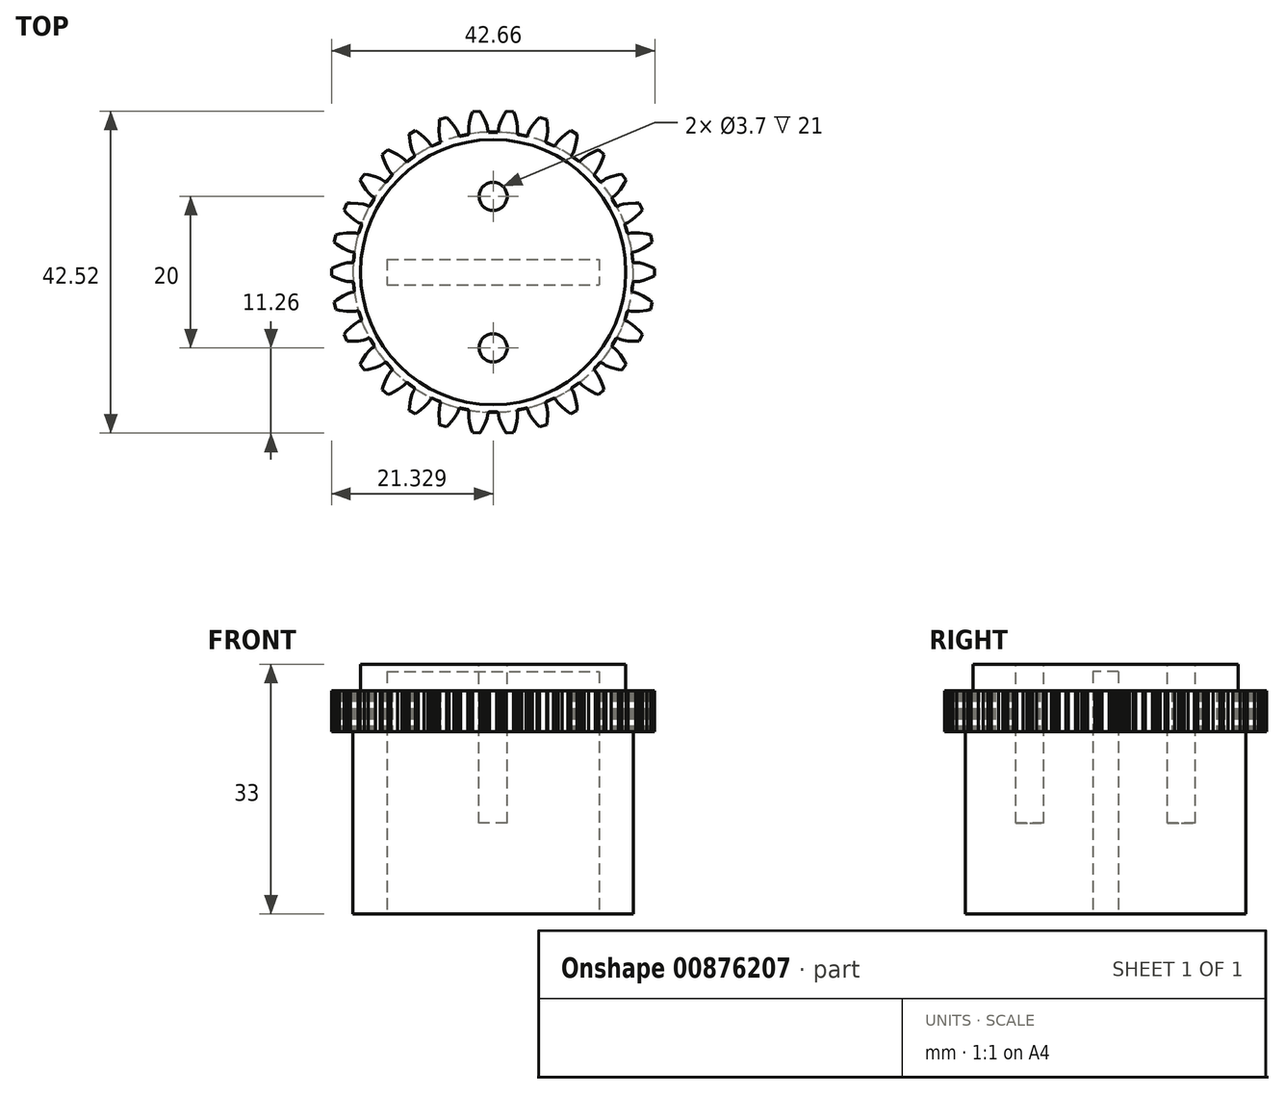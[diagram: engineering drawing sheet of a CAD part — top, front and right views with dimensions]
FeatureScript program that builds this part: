
annotation { "Feature Type Name" : "Feature", "Feature Type Description" : "" }
export const myFeature = defineFeature(function(context is Context, id is Id, definition is map)
    precondition{}
    {
        {
            var Q0;
            Q0=qCreatedBy(makeId("Top.planeOp"),FACE);
            var sketch = newSketch(context, id + "F0", { "sketchPlane" : qUnion([Q0])});
            skLineSegment(sketch, "E0", {"start": v(5.95, 16.64) * mm, "end": v(6.04, 16.7) * mm});
            skLineSegment(sketch, "E1", {"start": v(6.04, 16.7) * mm, "end": v(6.12, 16.74) * mm});
            skLineSegment(sketch, "E2", {"start": v(21.02, -17.09) * mm, "end": v(21.05, -17.07) * mm});
            skLineSegment(sketch, "E3", {"start": v(32.31, -2.53) * mm, "end": v(32.33, -2.41) * mm});
            skLineSegment(sketch, "E4", {"start": v(32.33, -2.41) * mm, "end": v(32.35, -2.32) * mm});
            skLineSegment(sketch, "E5", {"start": v(6.12, 16.74) * mm, "end": v(6.43, 16.86) * mm});
            skLineSegment(sketch, "E6", {"start": v(6.43, 16.86) * mm, "end": v(6.95, 17.06) * mm});
            skLineSegment(sketch, "E7", {"start": v(6.13, -16.74) * mm, "end": v(6.43, -16.86) * mm});
            skLineSegment(sketch, "E8", {"start": v(6.43, -16.86) * mm, "end": v(6.95, -17.06) * mm});
            skLineSegment(sketch, "E9", {"start": v(17.47, -18.17) * mm, "end": v(17.79, -18.09) * mm});
            skLineSegment(sketch, "E10", {"start": v(17.79, -18.09) * mm, "end": v(18.32, -17.95) * mm});
            skLineSegment(sketch, "E11", {"start": v(21.86, -16.75) * mm, "end": v(21.96, -16.7) * mm});
            skLineSegment(sketch, "E12", {"start": v(21.96, -16.7) * mm, "end": v(22.05, -16.64) * mm});
            skLineSegment(sketch, "E13", {"start": v(10.18, 18.1) * mm, "end": v(10.52, 18.17) * mm});
            skLineSegment(sketch, "E14", {"start": v(-4.35, 2.32) * mm, "end": v(-4.34, 2.41) * mm});
            skLineSegment(sketch, "E15", {"start": v(-4.34, 2.41) * mm, "end": v(-4.31, 2.53) * mm});
            skLineSegment(sketch, "E16", {"start": v(10.53, -18.17) * mm, "end": v(10.63, -18.18) * mm});
            skLineSegment(sketch, "E17", {"start": v(10.63, -18.18) * mm, "end": v(10.73, -18.2) * mm});
            skLineSegment(sketch, "E18", {"start": v(32.37, 1.98) * mm, "end": v(32.35, 2.27) * mm});
            skLineSegment(sketch, "E19", {"start": v(10.18, -18.1) * mm, "end": v(10.53, -18.17) * mm});
            skLineSegment(sketch, "E20", {"start": v(27.49, -12.66) * mm, "end": v(27.7, -12.4) * mm});
            skLineSegment(sketch, "E21", {"start": v(27.7, -12.4) * mm, "end": v(28.05, -11.98) * mm});
            skLineSegment(sketch, "E22", {"start": v(21.02, 17.09) * mm, "end": v(21.05, 17.07) * mm});
            skLineSegment(sketch, "E23", {"start": v(32.35, -2.27) * mm, "end": v(32.37, -1.98) * mm});
            skLineSegment(sketch, "E24", {"start": v(32.33, 2.41) * mm, "end": v(32.31, 2.52) * mm});
            skLineSegment(sketch, "E25", {"start": v(17.26, 18.2) * mm, "end": v(17.37, 18.18) * mm});
            skLineSegment(sketch, "E26", {"start": v(17.47, 18.17) * mm, "end": v(17.79, 18.09) * mm});
            skLineSegment(sketch, "E27", {"start": v(17.79, 18.09) * mm, "end": v(18.32, 17.95) * mm});
            skLineSegment(sketch, "E28", {"start": v(19.8, -20.1) * mm, "end": v(20.12, -20.44) * mm});
            skLineSegment(sketch, "E29", {"start": v(22.35, -17) * mm, "end": v(22.6, -17.33) * mm});
            skLineSegment(sketch, "E30", {"start": v(28.5, -15.07) * mm, "end": v(28.64, -15.52) * mm});
            skLineSegment(sketch, "E31", {"start": v(5.65, -17) * mm, "end": v(5.77, -16.76) * mm});
            skLineSegment(sketch, "E32", {"start": v(27.4, -13) * mm, "end": v(27.58, -13.2) * mm});
            skLineSegment(sketch, "E33", {"start": v(17.23, 18.66) * mm, "end": v(17.22, 19.08) * mm});
            skLineSegment(sketch, "E34", {"start": v(28.64, -15.52) * mm, "end": v(27.9, -16.18) * mm});
            skLineSegment(sketch, "E35", {"start": v(27.34, -12.9) * mm, "end": v(27.4, -13) * mm});
            skLineSegment(sketch, "E36", {"start": v(27.47, -16) * mm, "end": v(26.6, -15.55) * mm});
            skLineSegment(sketch, "E37", {"start": v(26.02, -15.16) * mm, "end": v(25.7, -14.88) * mm});
            skLineSegment(sketch, "E38", {"start": v(10.8, -18.28) * mm, "end": v(10.8, -18.4) * mm});
            skLineSegment(sketch, "E39", {"start": v(27.9, -16.18) * mm, "end": v(27.47, -16) * mm});
            skLineSegment(sketch, "E40", {"start": v(26.6, -15.55) * mm, "end": v(26.02, -15.16) * mm});
            skLineSegment(sketch, "E41", {"start": v(10.73, -18.2) * mm, "end": v(10.8, -18.28) * mm});
            skLineSegment(sketch, "E42", {"start": v(10.73, -18.2) * mm, "end": v(10.63, -18.15) * mm});
            skLineSegment(sketch, "E43", {"start": v(13.41, -18.48) * mm, "end": v(13.33, -18.55) * mm});
            skLineSegment(sketch, "E44", {"start": v(30.5, -8.72) * mm, "end": v(30.4, -8.7) * mm});
            skLineSegment(sketch, "E45", {"start": v(18.56, -18.1) * mm, "end": v(18.64, -18.36) * mm});
            skLineSegment(sketch, "E46", {"start": v(24.7, -16.12) * mm, "end": v(24.9, -16.8) * mm});
            skLineSegment(sketch, "E47", {"start": v(-5.77, -3.14) * mm, "end": v(-5.14, -2.83) * mm});
            skLineSegment(sketch, "E48", {"start": v(34.3, -5.02) * mm, "end": v(33.33, -5.17) * mm});
            skLineSegment(sketch, "E49", {"start": v(12.95, 19.99) * mm, "end": v(13.18, 19.33) * mm});
            skLineSegment(sketch, "E50", {"start": v(12.26, 21.26) * mm, "end": v(12.5, 20.86) * mm});
            skLineSegment(sketch, "E51", {"start": v(12.5, 20.86) * mm, "end": v(12.95, 19.99) * mm});
            skLineSegment(sketch, "E52", {"start": v(33.33, -5.17) * mm, "end": v(32.63, -5.2) * mm});
            skLineSegment(sketch, "E53", {"start": v(32.63, -5.2) * mm, "end": v(32.22, -5.16) * mm});
            skLineSegment(sketch, "E54", {"start": v(28.9, -12.33) * mm, "end": v(28.54, -12.12) * mm});
            skLineSegment(sketch, "E55", {"start": v(13.28, 18.92) * mm, "end": v(13.18, 19.33) * mm});
            skLineSegment(sketch, "E56", {"start": v(0.6, -12.7) * mm, "end": v(0.66, -12.8) * mm});
            skLineSegment(sketch, "E57", {"start": v(15.5, -20.86) * mm, "end": v(15.74, -21.26) * mm});
            skLineSegment(sketch, "E58", {"start": v(16.72, -21.16) * mm, "end": v(15.74, -21.26) * mm});
            skLineSegment(sketch, "E59", {"start": v(15.05, -19.99) * mm, "end": v(15.5, -20.86) * mm});
            skLineSegment(sketch, "E60", {"start": v(28.33, -11.96) * mm, "end": v(28.23, -11.92) * mm});
            skLineSegment(sketch, "E61", {"start": v(27.82, 13.54) * mm, "end": v(27.58, 13.2) * mm});
            skLineSegment(sketch, "E62", {"start": v(28.54, -12.12) * mm, "end": v(28.33, -11.96) * mm});
            skLineSegment(sketch, "E63", {"start": v(9.44, 18.1) * mm, "end": v(9.36, 18.36) * mm});
            skLineSegment(sketch, "E64", {"start": v(10.78, 19.08) * mm, "end": v(10.77, 18.66) * mm});
            skLineSegment(sketch, "E65", {"start": v(10.8, -18.4) * mm, "end": v(10.77, -18.66) * mm});
            skLineSegment(sketch, "E66", {"start": v(-4.3, -2.4) * mm, "end": v(-4.31, -2.52) * mm});
            skLineSegment(sketch, "E67", {"start": v(17.47, -18.17) * mm, "end": v(17.26, -18.2) * mm});
            skLineSegment(sketch, "E68", {"start": v(-4.36, -2.32) * mm, "end": v(-4.31, -2.52) * mm});
            skLineSegment(sketch, "E69", {"start": v(21.86, 16.75) * mm, "end": v(22.05, 16.64) * mm});
            skLineSegment(sketch, "E70", {"start": v(-4.36, -2.32) * mm, "end": v(-4.44, -1.35) * mm});
            skLineSegment(sketch, "E71", {"start": v(0.51, -12.66) * mm, "end": v(-0.12, -11.93) * mm});
            skLineSegment(sketch, "E72", {"start": v(30.21, -8.91) * mm, "end": v(29.7, -9.75) * mm});
            skLineSegment(sketch, "E73", {"start": v(30.5, 1.75) * mm, "end": v(30.5, -1.75) * mm, "construction": true});
            skLineSegment(sketch, "E74", {"start": v(27.48, 12.66) * mm, "end": v(27.34, 12.8) * mm});
            skLineSegment(sketch, "E75", {"start": v(0.51, 12.66) * mm, "end": v(0.66, 12.8) * mm});
            skLineSegment(sketch, "E76", {"start": v(27.49, -12.66) * mm, "end": v(27.34, -12.8) * mm});
            skLineSegment(sketch, "E77", {"start": v(-2.5, -1.75) * mm, "end": v(-2.5, 1.75) * mm, "construction": true});
            skLineSegment(sketch, "E78", {"start": v(-2.21, 8.9) * mm, "end": v(-1.7, 9.75) * mm});
            skLineSegment(sketch, "E79", {"start": v(0.51, -12.66) * mm, "end": v(0.66, -12.8) * mm});
            skLineSegment(sketch, "E80", {"start": v(30.21, 8.9) * mm, "end": v(29.74, 9.64) * mm});
            skLineSegment(sketch, "E81", {"start": v(30.21, -8.91) * mm, "end": v(30.3, -8.73) * mm});
            skLineSegment(sketch, "E82", {"start": v(10.52, 18.17) * mm, "end": v(10.73, 18.2) * mm});
            skLineSegment(sketch, "E83", {"start": v(17.23, -18.66) * mm, "end": v(17.2, -18.4) * mm});
            skLineSegment(sketch, "E84", {"start": v(-3.54, -12.14) * mm, "end": v(-3.32, -11.73) * mm});
            skLineSegment(sketch, "E85", {"start": v(30.4, 8.7) * mm, "end": v(30.5, 8.72) * mm});
            skLineSegment(sketch, "E86", {"start": v(-2.97, -12.93) * mm, "end": v(-3.54, -12.14) * mm});
            skLineSegment(sketch, "E87", {"start": v(-5.68, 8.23) * mm, "end": v(-5.38, 7.87) * mm});
            skLineSegment(sketch, "E88", {"start": v(21.12, 19.67) * mm, "end": v(21.17, 18.69) * mm});
            skLineSegment(sketch, "E89", {"start": v(9.36, 18.36) * mm, "end": v(9.18, 18.74) * mm});
            skLineSegment(sketch, "E90", {"start": v(-4.69, 7.18) * mm, "end": v(-5.38, 7.87) * mm});
            skLineSegment(sketch, "E91", {"start": v(31.85, 5.1) * mm, "end": v(31.96, 5.1) * mm});
            skLineSegment(sketch, "E92", {"start": v(-2.97, 12.93) * mm, "end": v(-2.5, 12.85) * mm});
            skLineSegment(sketch, "E93", {"start": v(28.23, -11.92) * mm, "end": v(28.12, -11.93) * mm});
            skLineSegment(sketch, "E94", {"start": v(34.6, 3.67) * mm, "end": v(33.77, 3.14) * mm});
            skLineSegment(sketch, "E95", {"start": v(31.39, -6.27) * mm, "end": v(31.43, -6.37) * mm});
            skLineSegment(sketch, "E96", {"start": v(12.95, -19.99) * mm, "end": v(12.5, -20.86) * mm});
            skLineSegment(sketch, "E97", {"start": v(10.63, 18.15) * mm, "end": v(10.73, 18.2) * mm});
            skLineSegment(sketch, "E98", {"start": v(3.3, 16.12) * mm, "end": v(3.46, 15.73) * mm});
            skLineSegment(sketch, "E99", {"start": v(21.12, 18) * mm, "end": v(21.04, 17.58) * mm});
            skLineSegment(sketch, "E100", {"start": v(34.96, 3.95) * mm, "end": v(34.6, 3.67) * mm});
            skLineSegment(sketch, "E101", {"start": v(-4.31, 2.53) * mm, "end": v(-4.3, 2.4) * mm});
            skLineSegment(sketch, "E102", {"start": v(20.95, -17.33) * mm, "end": v(20.93, -17.22) * mm});
            skLineSegment(sketch, "E103", {"start": v(24.4, -15.5) * mm, "end": v(24.36, -15.4) * mm});
            skLineSegment(sketch, "E104", {"start": v(9.36, -18.36) * mm, "end": v(9.44, -18.1) * mm});
            skLineSegment(sketch, "E105", {"start": v(13.28, -18.92) * mm, "end": v(13.3, -18.65) * mm});
            skLineSegment(sketch, "E106", {"start": v(17.2, -18.4) * mm, "end": v(17.2, -18.28) * mm});
            skLineSegment(sketch, "E107", {"start": v(27.39, 12.7) * mm, "end": v(27.34, 12.8) * mm});
            skLineSegment(sketch, "E108", {"start": v(5.65, 17) * mm, "end": v(5.4, 17.33) * mm});
            skLineSegment(sketch, "E109", {"start": v(17.2, 18.28) * mm, "end": v(17.2, 18.4) * mm});
            skLineSegment(sketch, "E110", {"start": v(10.7, 17.33) * mm, "end": v(8.55, 16.78) * mm});
            skLineSegment(sketch, "E111", {"start": v(17.3, 17.33) * mm, "end": v(15.1, 17.6) * mm});
            skLineSegment(sketch, "E112", {"start": v(8.55, 16.78) * mm, "end": v(6.49, 15.96) * mm});
            skLineSegment(sketch, "E113", {"start": v(15.1, 17.6) * mm, "end": v(12.9, 17.6) * mm});
            skLineSegment(sketch, "E114", {"start": v(19.45, 16.78) * mm, "end": v(17.3, 17.33) * mm});
            skLineSegment(sketch, "E115", {"start": v(12.9, 17.6) * mm, "end": v(10.7, 17.33) * mm});
            skLineSegment(sketch, "E116", {"start": v(23.1, 17.83) * mm, "end": v(22.6, 17.33) * mm});
            skLineSegment(sketch, "E117", {"start": v(20.93, 17.22) * mm, "end": v(20.95, 17.33) * mm});
            skLineSegment(sketch, "E118", {"start": v(30.5, 1.75) * mm, "end": v(-2.5, 1.75) * mm, "construction": true});
            skLineSegment(sketch, "E119", {"start": v(22.05, 16.64) * mm, "end": v(21.94, 16.66) * mm});
            skLineSegment(sketch, "E120", {"start": v(22.6, 17.33) * mm, "end": v(22.35, 17) * mm});
            skLineSegment(sketch, "E121", {"start": v(-2.5, -1.75) * mm, "end": v(30.5, -1.75) * mm, "construction": true});
            skLineSegment(sketch, "E122", {"start": v(21.94, 16.66) * mm, "end": v(21.05, 17.07) * mm});
            skLineSegment(sketch, "E123", {"start": v(22.15, 16.67) * mm, "end": v(22.05, 16.64) * mm});
            skLineSegment(sketch, "E124", {"start": v(22.22, 16.76) * mm, "end": v(22.15, 16.67) * mm});
            skLineSegment(sketch, "E125", {"start": v(22.35, 17) * mm, "end": v(22.22, 16.76) * mm});
            skLineSegment(sketch, "E126", {"start": v(20.98, 17.12) * mm, "end": v(20.93, 17.22) * mm});
            skLineSegment(sketch, "E127", {"start": v(23.85, 18.45) * mm, "end": v(23.1, 17.83) * mm});
            skLineSegment(sketch, "E128", {"start": v(24.24, 18.72) * mm, "end": v(23.85, 18.45) * mm});
            skLineSegment(sketch, "E129", {"start": v(26.02, 15.16) * mm, "end": v(25.7, 14.88) * mm});
            skLineSegment(sketch, "E130", {"start": v(26.6, 15.55) * mm, "end": v(26.02, 15.16) * mm});
            skLineSegment(sketch, "E131", {"start": v(24.38, 15.3) * mm, "end": v(24.36, 15.4) * mm});
            skLineSegment(sketch, "E132", {"start": v(25.05, 17.76) * mm, "end": v(25.09, 18.22) * mm});
            skLineSegment(sketch, "E133", {"start": v(24.54, 15.73) * mm, "end": v(24.7, 16.12) * mm});
            skLineSegment(sketch, "E134", {"start": v(24.36, 15.4) * mm, "end": v(24.4, 15.5) * mm});
            skLineSegment(sketch, "E135", {"start": v(24.4, 15.5) * mm, "end": v(24.54, 15.73) * mm});
            skLineSegment(sketch, "E136", {"start": v(24.9, 16.8) * mm, "end": v(25.05, 17.76) * mm});
            skLineSegment(sketch, "E137", {"start": v(25.23, 14.64) * mm, "end": v(24.46, 15.21) * mm});
            skLineSegment(sketch, "E138", {"start": v(25.09, 18.22) * mm, "end": v(24.24, 18.72) * mm});
            skLineSegment(sketch, "E139", {"start": v(24.7, 16.12) * mm, "end": v(24.9, 16.8) * mm});
            skLineSegment(sketch, "E140", {"start": v(25.44, 14.62) * mm, "end": v(25.33, 14.6) * mm});
            skLineSegment(sketch, "E141", {"start": v(25.53, 14.68) * mm, "end": v(25.44, 14.62) * mm});
            skLineSegment(sketch, "E142", {"start": v(25.7, 14.88) * mm, "end": v(25.53, 14.68) * mm});
            skLineSegment(sketch, "E143", {"start": v(-2.33, -10.37) * mm, "end": v(-2.78, -10.9) * mm});
            skLineSegment(sketch, "E144", {"start": v(21.12, 19.67) * mm, "end": v(21.06, 20.13) * mm});
            skLineSegment(sketch, "E145", {"start": v(-2.03, -10.08) * mm, "end": v(-2.33, -10.37) * mm});
            skLineSegment(sketch, "E146", {"start": v(20.95, 17.33) * mm, "end": v(21.04, 17.58) * mm});
            skLineSegment(sketch, "E147", {"start": v(3.64, -15.4) * mm, "end": v(3.6, -15.5) * mm});
            skLineSegment(sketch, "E148", {"start": v(13.18, -19.33) * mm, "end": v(13.28, -18.92) * mm});
            skLineSegment(sketch, "E149", {"start": v(27.47, 16) * mm, "end": v(26.6, 15.55) * mm});
            skLineSegment(sketch, "E150", {"start": v(6.95, -17.06) * mm, "end": v(7.02, -17.12) * mm});
            skLineSegment(sketch, "E151", {"start": v(32.68, -7.18) * mm, "end": v(32.13, -6.75) * mm});
            skLineSegment(sketch, "E152", {"start": v(19.8, 20.1) * mm, "end": v(19.19, 19.33) * mm});
            skLineSegment(sketch, "E153", {"start": v(20.12, 20.44) * mm, "end": v(19.8, 20.1) * mm});
            skLineSegment(sketch, "E154", {"start": v(32.13, -6.75) * mm, "end": v(31.77, -6.53) * mm});
            skLineSegment(sketch, "E155", {"start": v(21.06, 20.13) * mm, "end": v(20.12, 20.44) * mm});
            skLineSegment(sketch, "E156", {"start": v(21.12, 18) * mm, "end": v(21.17, 18.69) * mm});
            skLineSegment(sketch, "E157", {"start": v(13.3, -18.65) * mm, "end": v(13.33, -18.55) * mm});
            skLineSegment(sketch, "E158", {"start": v(21.94, -16.66) * mm, "end": v(22.05, -16.64) * mm});
            skLineSegment(sketch, "E159", {"start": v(-1.8, -9.93) * mm, "end": v(-2.03, -10.08) * mm});
            skLineSegment(sketch, "E160", {"start": v(18.64, 18.36) * mm, "end": v(18.56, 18.1) * mm});
            skLineSegment(sketch, "E161", {"start": v(22.05, -16.64) * mm, "end": v(22.15, -16.67) * mm});
            skLineSegment(sketch, "E162", {"start": v(18.82, 18.74) * mm, "end": v(18.64, 18.36) * mm});
            skLineSegment(sketch, "E163", {"start": v(7.02, -17.12) * mm, "end": v(7.06, -17.22) * mm});
            skLineSegment(sketch, "E164", {"start": v(17.36, 18.15) * mm, "end": v(17.26, 18.2) * mm});
            skLineSegment(sketch, "E165", {"start": v(17.2, -18.28) * mm, "end": v(17.26, -18.2) * mm});
            skLineSegment(sketch, "E166", {"start": v(19.19, 19.33) * mm, "end": v(18.82, 18.74) * mm});
            skLineSegment(sketch, "E167", {"start": v(18.42, 17.95) * mm, "end": v(18.32, 17.95) * mm});
            skLineSegment(sketch, "E168", {"start": v(18.5, 18) * mm, "end": v(18.42, 17.95) * mm});
            skLineSegment(sketch, "E169", {"start": v(18.56, 18.1) * mm, "end": v(18.5, 18) * mm});
            skLineSegment(sketch, "E170", {"start": v(22.15, -16.67) * mm, "end": v(22.22, -16.76) * mm});
            skLineSegment(sketch, "E171", {"start": v(33.38, -7.87) * mm, "end": v(32.68, -7.18) * mm});
            skLineSegment(sketch, "E172", {"start": v(17.26, 18.2) * mm, "end": v(17.2, 18.28) * mm});
            skLineSegment(sketch, "E173", {"start": v(21.05, -17.07) * mm, "end": v(21.94, -16.66) * mm});
            skLineSegment(sketch, "E174", {"start": v(21.04, -17.58) * mm, "end": v(20.95, -17.33) * mm});
            skLineSegment(sketch, "E175", {"start": v(21.17, -18.69) * mm, "end": v(21.12, -18) * mm});
            skLineSegment(sketch, "E176", {"start": v(17.2, 18.4) * mm, "end": v(17.23, 18.66) * mm});
            skLineSegment(sketch, "E177", {"start": v(20.93, -17.22) * mm, "end": v(20.98, -17.12) * mm});
            skLineSegment(sketch, "E178", {"start": v(14.48, 18.45) * mm, "end": v(13.52, 18.45) * mm});
            skLineSegment(sketch, "E179", {"start": v(14.7, 18.65) * mm, "end": v(14.67, 18.55) * mm});
            skLineSegment(sketch, "E180", {"start": v(14.72, 18.92) * mm, "end": v(14.7, 18.65) * mm});
            skLineSegment(sketch, "E181", {"start": v(14.81, 19.33) * mm, "end": v(14.72, 18.92) * mm});
            skLineSegment(sketch, "E182", {"start": v(15.05, 19.99) * mm, "end": v(14.81, 19.33) * mm});
            skLineSegment(sketch, "E183", {"start": v(21.12, -18) * mm, "end": v(21.04, -17.58) * mm});
            skLineSegment(sketch, "E184", {"start": v(14.67, 18.55) * mm, "end": v(14.59, 18.48) * mm});
            skLineSegment(sketch, "E185", {"start": v(25.09, -18.22) * mm, "end": v(25.05, -17.76) * mm});
            skLineSegment(sketch, "E186", {"start": v(16.87, 20.72) * mm, "end": v(16.72, 21.16) * mm});
            skLineSegment(sketch, "E187", {"start": v(13.3, 18.65) * mm, "end": v(13.28, 18.92) * mm});
            skLineSegment(sketch, "E188", {"start": v(31.75, -5.15) * mm, "end": v(31.85, -5.1) * mm});
            skLineSegment(sketch, "E189", {"start": v(11.12, 20.72) * mm, "end": v(10.87, 19.77) * mm});
            skLineSegment(sketch, "E190", {"start": v(12.26, 21.26) * mm, "end": v(11.28, 21.16) * mm});
            skLineSegment(sketch, "E191", {"start": v(10.87, 19.77) * mm, "end": v(10.78, 19.08) * mm});
            skLineSegment(sketch, "E192", {"start": v(33.68, -8.23) * mm, "end": v(33.38, -7.87) * mm});
            skLineSegment(sketch, "E193", {"start": v(15.74, 21.26) * mm, "end": v(15.5, 20.86) * mm});
            skLineSegment(sketch, "E194", {"start": v(17.12, 19.77) * mm, "end": v(16.87, 20.72) * mm});
            skLineSegment(sketch, "E195", {"start": v(11.28, 21.16) * mm, "end": v(11.12, 20.72) * mm});
            skLineSegment(sketch, "E196", {"start": v(15.5, 20.86) * mm, "end": v(15.05, 19.99) * mm});
            skLineSegment(sketch, "E197", {"start": v(13.33, 18.55) * mm, "end": v(13.3, 18.65) * mm});
            skLineSegment(sketch, "E198", {"start": v(16.72, 21.16) * mm, "end": v(15.74, 21.26) * mm});
            skLineSegment(sketch, "E199", {"start": v(11.28, -21.16) * mm, "end": v(12.26, -21.26) * mm});
            skLineSegment(sketch, "E200", {"start": v(27.34, -12.8) * mm, "end": v(27.39, -12.7) * mm});
            skLineSegment(sketch, "E201", {"start": v(10.8, 18.28) * mm, "end": v(10.73, 18.2) * mm});
            skLineSegment(sketch, "E202", {"start": v(10.8, 18.4) * mm, "end": v(10.8, 18.28) * mm});
            skLineSegment(sketch, "E203", {"start": v(11.12, -20.72) * mm, "end": v(11.28, -21.16) * mm});
            skLineSegment(sketch, "E204", {"start": v(10.77, 18.66) * mm, "end": v(10.8, 18.4) * mm});
            skLineSegment(sketch, "E205", {"start": v(3.6, -15.5) * mm, "end": v(3.46, -15.73) * mm});
            skLineSegment(sketch, "E206", {"start": v(-6.9, -0.7) * mm, "end": v(-6, -1.04) * mm});
            skLineSegment(sketch, "E207", {"start": v(-6.9, 0.7) * mm, "end": v(-7.33, 0.5) * mm});
            skLineSegment(sketch, "E208", {"start": v(10.87, -19.77) * mm, "end": v(11.12, -20.72) * mm});
            skLineSegment(sketch, "E209", {"start": v(10.78, -19.08) * mm, "end": v(10.87, -19.77) * mm});
            skLineSegment(sketch, "E210", {"start": v(12.26, -21.26) * mm, "end": v(12.5, -20.86) * mm});
            skLineSegment(sketch, "E211", {"start": v(-7.33, -0.5) * mm, "end": v(-6.9, -0.7) * mm});
            skLineSegment(sketch, "E212", {"start": v(23.85, -18.45) * mm, "end": v(24.24, -18.72) * mm});
            skLineSegment(sketch, "E213", {"start": v(9.58, 17.95) * mm, "end": v(9.49, 18) * mm});
            skLineSegment(sketch, "E214", {"start": v(-7.33, 0.5) * mm, "end": v(-7.33, -0.5) * mm});
            skLineSegment(sketch, "E215", {"start": v(-4.22, -5.16) * mm, "end": v(-3.96, -5.1) * mm});
            skLineSegment(sketch, "E216", {"start": v(3.46, -15.73) * mm, "end": v(3.3, -16.12) * mm});
            skLineSegment(sketch, "E217", {"start": v(-3.7, -5.24) * mm, "end": v(-3.4, -6.16) * mm});
            skLineSegment(sketch, "E218", {"start": v(-5.38, -7.87) * mm, "end": v(-5.68, -8.23) * mm});
            skLineSegment(sketch, "E219", {"start": v(9.49, 18) * mm, "end": v(9.44, 18.1) * mm});
            skLineSegment(sketch, "E220", {"start": v(-3.85, -5.1) * mm, "end": v(-3.75, -5.15) * mm});
            skLineSegment(sketch, "E221", {"start": v(-5.3, 1.2) * mm, "end": v(-6, 1.04) * mm});
            skLineSegment(sketch, "E222", {"start": v(-6, 1.04) * mm, "end": v(-6.9, 0.7) * mm});
            skLineSegment(sketch, "E223", {"start": v(8.81, 19.33) * mm, "end": v(8.2, 20.1) * mm});
            skLineSegment(sketch, "E224", {"start": v(3.3, -16.12) * mm, "end": v(3.1, -16.8) * mm});
            skLineSegment(sketch, "E225", {"start": v(9.18, 18.74) * mm, "end": v(8.81, 19.33) * mm});
            skLineSegment(sketch, "E226", {"start": v(-5.68, -8.23) * mm, "end": v(-5.28, -9.12) * mm});
            skLineSegment(sketch, "E227", {"start": v(-3.96, -5.1) * mm, "end": v(-3.85, -5.1) * mm});
            skLineSegment(sketch, "E228", {"start": v(7.88, 20.44) * mm, "end": v(6.94, 20.13) * mm});
            skLineSegment(sketch, "E229", {"start": v(-4.31, -2.52) * mm, "end": v(-4.38, -2.6) * mm});
            skLineSegment(sketch, "E230", {"start": v(-4.4, 1.45) * mm, "end": v(-4.44, 1.35) * mm});
            skLineSegment(sketch, "E231", {"start": v(-4.74, -2.7) * mm, "end": v(-5.14, -2.83) * mm});
            skLineSegment(sketch, "E232", {"start": v(2.95, 17.76) * mm, "end": v(3.1, 16.8) * mm});
            skLineSegment(sketch, "E233", {"start": v(5.95, -16.64) * mm, "end": v(6.05, -16.66) * mm});
            skLineSegment(sketch, "E234", {"start": v(-4.48, -2.65) * mm, "end": v(-4.74, -2.7) * mm});
            skLineSegment(sketch, "E235", {"start": v(-4.38, -2.6) * mm, "end": v(-4.48, -2.65) * mm});
            skLineSegment(sketch, "E236", {"start": v(-4.44, 1.35) * mm, "end": v(-4.52, 1.28) * mm});
            skLineSegment(sketch, "E237", {"start": v(-5.14, 2.83) * mm, "end": v(-4.74, 2.7) * mm});
            skLineSegment(sketch, "E238", {"start": v(-4.52, 1.28) * mm, "end": v(-4.63, 1.25) * mm});
            skLineSegment(sketch, "E239", {"start": v(-6, -1.04) * mm, "end": v(-5.3, -1.2) * mm});
            skLineSegment(sketch, "E240", {"start": v(14.59, -18.48) * mm, "end": v(14.67, -18.55) * mm});
            skLineSegment(sketch, "E241", {"start": v(30.22, -8.8) * mm, "end": v(30.3, -8.73) * mm});
            skLineSegment(sketch, "E242", {"start": v(2.95, -17.76) * mm, "end": v(2.9, -18.22) * mm});
            skLineSegment(sketch, "E243", {"start": v(29.7, -9.75) * mm, "end": v(29.74, -9.64) * mm});
            skLineSegment(sketch, "E244", {"start": v(3.1, -16.8) * mm, "end": v(2.95, -17.76) * mm});
            skLineSegment(sketch, "E245", {"start": v(5.77, -16.76) * mm, "end": v(5.84, -16.67) * mm});
            skLineSegment(sketch, "E246", {"start": v(8.2, 20.1) * mm, "end": v(7.88, 20.44) * mm});
            skLineSegment(sketch, "E247", {"start": v(3.54, 15.21) * mm, "end": v(2.76, 14.64) * mm});
            skLineSegment(sketch, "E248", {"start": v(3.64, 15.4) * mm, "end": v(3.61, 15.3) * mm});
            skLineSegment(sketch, "E249", {"start": v(3.6, 15.5) * mm, "end": v(3.64, 15.4) * mm});
            skLineSegment(sketch, "E250", {"start": v(-5.3, -1.2) * mm, "end": v(-4.9, -1.26) * mm});
            skLineSegment(sketch, "E251", {"start": v(30.3, -8.73) * mm, "end": v(30.4, -8.7) * mm});
            skLineSegment(sketch, "E252", {"start": v(29.74, -9.64) * mm, "end": v(30.22, -8.8) * mm});
            skLineSegment(sketch, "E253", {"start": v(3.76, 18.72) * mm, "end": v(2.9, 18.22) * mm});
            skLineSegment(sketch, "E254", {"start": v(6.88, 19.67) * mm, "end": v(6.83, 18.69) * mm});
            skLineSegment(sketch, "E255", {"start": v(-5.34, -5.17) * mm, "end": v(-4.64, -5.2) * mm});
            skLineSegment(sketch, "E256", {"start": v(4.15, 18.45) * mm, "end": v(3.76, 18.72) * mm});
            skLineSegment(sketch, "E257", {"start": v(18.5, -18) * mm, "end": v(18.56, -18.1) * mm});
            skLineSegment(sketch, "E258", {"start": v(18.42, -17.95) * mm, "end": v(18.5, -18) * mm});
            skLineSegment(sketch, "E259", {"start": v(-6.76, -4.92) * mm, "end": v(-6.3, -5.02) * mm});
            skLineSegment(sketch, "E260", {"start": v(3.46, 15.73) * mm, "end": v(3.6, 15.5) * mm});
            skLineSegment(sketch, "E261", {"start": v(2.9, 18.22) * mm, "end": v(2.95, 17.76) * mm});
            skLineSegment(sketch, "E262", {"start": v(4.9, 17.83) * mm, "end": v(4.15, 18.45) * mm});
            skLineSegment(sketch, "E263", {"start": v(17.26, -18.2) * mm, "end": v(17.36, -18.15) * mm});
            skLineSegment(sketch, "E264", {"start": v(-4.64, -5.2) * mm, "end": v(-4.22, -5.16) * mm});
            skLineSegment(sketch, "E265", {"start": v(-6.3, -5.02) * mm, "end": v(-5.34, -5.17) * mm});
            skLineSegment(sketch, "E266", {"start": v(18.32, -17.95) * mm, "end": v(18.42, -17.95) * mm});
            skLineSegment(sketch, "E267", {"start": v(3.1, 16.8) * mm, "end": v(3.3, 16.12) * mm});
            skLineSegment(sketch, "E268", {"start": v(6.94, 20.13) * mm, "end": v(6.88, 19.67) * mm});
            skLineSegment(sketch, "E269", {"start": v(-0.04, 11.99) * mm, "end": v(-0.12, 11.93) * mm});
            skLineSegment(sketch, "E270", {"start": v(0.66, 12.8) * mm, "end": v(0.6, 12.7) * mm});
            skLineSegment(sketch, "E271", {"start": v(-4.63, -1.25) * mm, "end": v(-4.52, -1.28) * mm});
            skLineSegment(sketch, "E272", {"start": v(0.66, 12.9) * mm, "end": v(0.66, 12.8) * mm});
            skLineSegment(sketch, "E273", {"start": v(-4.9, -1.26) * mm, "end": v(-4.63, -1.25) * mm});
            skLineSegment(sketch, "E274", {"start": v(-2.97, 12.93) * mm, "end": v(-3.54, 12.14) * mm});
            skLineSegment(sketch, "E275", {"start": v(-0.23, 11.92) * mm, "end": v(-0.33, 11.96) * mm});
            skLineSegment(sketch, "E276", {"start": v(-3.54, 12.14) * mm, "end": v(-3.32, 11.73) * mm});
            skLineSegment(sketch, "E277", {"start": v(2.66, 14.6) * mm, "end": v(2.56, 14.62) * mm});
            skLineSegment(sketch, "E278", {"start": v(-4.69, -7.18) * mm, "end": v(-5.38, -7.87) * mm});
            skLineSegment(sketch, "E279", {"start": v(-0.12, 11.93) * mm, "end": v(-0.23, 11.92) * mm});
            skLineSegment(sketch, "E280", {"start": v(-4.52, -1.28) * mm, "end": v(-4.44, -1.35) * mm});
            skLineSegment(sketch, "E281", {"start": v(5.84, 16.67) * mm, "end": v(5.77, 16.76) * mm});
            skLineSegment(sketch, "E282", {"start": v(-2.3, 8.73) * mm, "end": v(-2.4, 8.7) * mm});
            skLineSegment(sketch, "E283", {"start": v(-1.73, 9.85) * mm, "end": v(-1.7, 9.75) * mm});
            skLineSegment(sketch, "E284", {"start": v(-3.84, 9.08) * mm, "end": v(-4.82, 9.14) * mm});
            skLineSegment(sketch, "E285", {"start": v(6.05, 16.66) * mm, "end": v(5.95, 16.64) * mm});
            skLineSegment(sketch, "E286", {"start": v(-2.22, 8.8) * mm, "end": v(-2.3, 8.73) * mm});
            skLineSegment(sketch, "E287", {"start": v(-1.7, 9.75) * mm, "end": v(-1.74, 9.64) * mm});
            skLineSegment(sketch, "E288", {"start": v(-1.8, 9.93) * mm, "end": v(-1.73, 9.85) * mm});
            skLineSegment(sketch, "E289", {"start": v(7.06, 17.22) * mm, "end": v(7.02, 17.12) * mm});
            skLineSegment(sketch, "E290", {"start": v(-2.5, 8.72) * mm, "end": v(-2.75, 8.84) * mm});
            skLineSegment(sketch, "E291", {"start": v(-3.15, 8.96) * mm, "end": v(-3.84, 9.08) * mm});
            skLineSegment(sketch, "E292", {"start": v(-2.75, 8.84) * mm, "end": v(-3.15, 8.96) * mm});
            skLineSegment(sketch, "E293", {"start": v(5.95, 16.64) * mm, "end": v(5.84, 16.67) * mm});
            skLineSegment(sketch, "E294", {"start": v(7.02, 17.12) * mm, "end": v(6.95, 17.06) * mm});
            skLineSegment(sketch, "E295", {"start": v(-2.4, 8.7) * mm, "end": v(-2.5, 8.72) * mm});
            skLineSegment(sketch, "E296", {"start": v(-5.77, 3.14) * mm, "end": v(-5.14, 2.83) * mm});
            skLineSegment(sketch, "E297", {"start": v(-3.32, 11.73) * mm, "end": v(-2.78, 10.9) * mm});
            skLineSegment(sketch, "E298", {"start": v(-6.3, 5.02) * mm, "end": v(-6.76, 4.92) * mm});
            skLineSegment(sketch, "E299", {"start": v(-4.38, 2.6) * mm, "end": v(-4.31, 2.53) * mm});
            skLineSegment(sketch, "E300", {"start": v(-4.64, 5.2) * mm, "end": v(-5.34, 5.17) * mm});
            skLineSegment(sketch, "E301", {"start": v(-2.03, 10.08) * mm, "end": v(-1.8, 9.93) * mm});
            skLineSegment(sketch, "E302", {"start": v(-2.78, 10.9) * mm, "end": v(-2.33, 10.37) * mm});
            skLineSegment(sketch, "E303", {"start": v(-4.63, 1.25) * mm, "end": v(-4.9, 1.26) * mm});
            skLineSegment(sketch, "E304", {"start": v(-4.74, 2.7) * mm, "end": v(-4.48, 2.65) * mm});
            skLineSegment(sketch, "E305", {"start": v(-4.82, 9.14) * mm, "end": v(-5.28, 9.12) * mm});
            skLineSegment(sketch, "E306", {"start": v(-6.96, 3.95) * mm, "end": v(-6.6, 3.67) * mm});
            skLineSegment(sketch, "E307", {"start": v(-6.76, 4.92) * mm, "end": v(-6.96, 3.95) * mm});
            skLineSegment(sketch, "E308", {"start": v(-2.33, 10.37) * mm, "end": v(-2.03, 10.08) * mm});
            skLineSegment(sketch, "E309", {"start": v(-6.6, 3.67) * mm, "end": v(-5.77, 3.14) * mm});
            skLineSegment(sketch, "E310", {"start": v(-5.34, 5.17) * mm, "end": v(-6.3, 5.02) * mm});
            skLineSegment(sketch, "E311", {"start": v(-4.48, 2.65) * mm, "end": v(-4.38, 2.6) * mm});
            skLineSegment(sketch, "E312", {"start": v(-4.13, 6.75) * mm, "end": v(-3.77, 6.53) * mm});
            skLineSegment(sketch, "E313", {"start": v(1.98, 15.16) * mm, "end": v(1.4, 15.55) * mm});
            skLineSegment(sketch, "E314", {"start": v(-3.44, 6.37) * mm, "end": v(-3.4, 6.27) * mm});
            skLineSegment(sketch, "E315", {"start": v(-3.85, 5.1) * mm, "end": v(-3.96, 5.1) * mm});
            skLineSegment(sketch, "E316", {"start": v(-3.4, 6.16) * mm, "end": v(-3.7, 5.24) * mm});
            skLineSegment(sketch, "E317", {"start": v(-3.96, 5.1) * mm, "end": v(-4.22, 5.16) * mm});
            skLineSegment(sketch, "E318", {"start": v(-3.77, 6.53) * mm, "end": v(-3.53, 6.43) * mm});
            skLineSegment(sketch, "E319", {"start": v(-3.53, 6.43) * mm, "end": v(-3.44, 6.37) * mm});
            skLineSegment(sketch, "E320", {"start": v(-4.22, 5.16) * mm, "end": v(-4.64, 5.2) * mm});
            skLineSegment(sketch, "E321", {"start": v(-4.69, 7.18) * mm, "end": v(-4.13, 6.75) * mm});
            skLineSegment(sketch, "E322", {"start": v(-3.75, 5.15) * mm, "end": v(-3.85, 5.1) * mm});
            skLineSegment(sketch, "E323", {"start": v(-0.12, -11.93) * mm, "end": v(-0.04, -11.99) * mm});
            skLineSegment(sketch, "E324", {"start": v(2.3, 14.88) * mm, "end": v(1.98, 15.16) * mm});
            skLineSegment(sketch, "E325", {"start": v(0.52, 16) * mm, "end": v(0.1, 16.18) * mm});
            skLineSegment(sketch, "E326", {"start": v(2.9, -18.22) * mm, "end": v(3.76, -18.72) * mm});
            skLineSegment(sketch, "E327", {"start": v(-0.15, 14.16) * mm, "end": v(0.18, 13.54) * mm});
            skLineSegment(sketch, "E328", {"start": v(0.42, 13.2) * mm, "end": v(0.6, 13) * mm});
            skLineSegment(sketch, "E329", {"start": v(-2.4, -8.7) * mm, "end": v(-2.3, -8.73) * mm});
            skLineSegment(sketch, "E330", {"start": v(0.6, 13) * mm, "end": v(0.66, 12.9) * mm});
            skLineSegment(sketch, "E331", {"start": v(-2.75, -8.84) * mm, "end": v(-2.5, -8.72) * mm});
            skLineSegment(sketch, "E332", {"start": v(2.47, 14.68) * mm, "end": v(2.3, 14.88) * mm});
            skLineSegment(sketch, "E333", {"start": v(-2.5, -8.72) * mm, "end": v(-2.4, -8.7) * mm});
            skLineSegment(sketch, "E334", {"start": v(0.18, 13.54) * mm, "end": v(0.42, 13.2) * mm});
            skLineSegment(sketch, "E335", {"start": v(-0.5, 15.07) * mm, "end": v(-0.15, 14.16) * mm});
            skLineSegment(sketch, "E336", {"start": v(3.76, -18.72) * mm, "end": v(4.15, -18.45) * mm});
            skLineSegment(sketch, "E337", {"start": v(-2.3, -8.73) * mm, "end": v(-2.22, -8.8) * mm});
            skLineSegment(sketch, "E338", {"start": v(-0.64, 15.52) * mm, "end": v(-0.5, 15.07) * mm});
            skLineSegment(sketch, "E339", {"start": v(7.05, 17.33) * mm, "end": v(7.06, 17.22) * mm});
            skLineSegment(sketch, "E340", {"start": v(6.96, 17.58) * mm, "end": v(7.05, 17.33) * mm});
            skLineSegment(sketch, "E341", {"start": v(7.06, -17.22) * mm, "end": v(7.05, -17.33) * mm});
            skLineSegment(sketch, "E342", {"start": v(6.83, -18.69) * mm, "end": v(6.88, -19.67) * mm});
            skLineSegment(sketch, "E343", {"start": v(6.96, -17.58) * mm, "end": v(6.88, -18) * mm});
            skLineSegment(sketch, "E344", {"start": v(6.94, -20.13) * mm, "end": v(7.88, -20.44) * mm});
            skLineSegment(sketch, "E345", {"start": v(-3.84, -9.08) * mm, "end": v(-3.15, -8.96) * mm});
            skLineSegment(sketch, "E346", {"start": v(6.88, -19.67) * mm, "end": v(6.94, -20.13) * mm});
            skLineSegment(sketch, "E347", {"start": v(34.76, -4.92) * mm, "end": v(34.96, -3.95) * mm});
            skLineSegment(sketch, "E348", {"start": v(6.88, -18) * mm, "end": v(6.83, -18.69) * mm});
            skLineSegment(sketch, "E349", {"start": v(-5.28, -9.12) * mm, "end": v(-4.82, -9.14) * mm});
            skLineSegment(sketch, "E350", {"start": v(31.85, -5.1) * mm, "end": v(31.96, -5.1) * mm});
            skLineSegment(sketch, "E351", {"start": v(-3.15, -8.96) * mm, "end": v(-2.75, -8.84) * mm});
            skLineSegment(sketch, "E352", {"start": v(7.05, -17.33) * mm, "end": v(6.96, -17.58) * mm});
            skLineSegment(sketch, "E353", {"start": v(22.6, -17.33) * mm, "end": v(23.1, -17.83) * mm});
            skLineSegment(sketch, "E354", {"start": v(23.1, -17.83) * mm, "end": v(23.85, -18.45) * mm});
            skLineSegment(sketch, "E355", {"start": v(-4.82, -9.14) * mm, "end": v(-3.84, -9.08) * mm});
            skLineSegment(sketch, "E356", {"start": v(-5.28, 9.12) * mm, "end": v(-5.68, 8.23) * mm});
            skLineSegment(sketch, "E357", {"start": v(-3.09, 4.39) * mm, "end": v(-3.5, 2.21) * mm});
            skLineSegment(sketch, "E358", {"start": v(2.75, -13.6) * mm, "end": v(4.55, -14.9) * mm});
            skLineSegment(sketch, "E359", {"start": v(4.15, -18.45) * mm, "end": v(4.9, -17.83) * mm});
            skLineSegment(sketch, "E360", {"start": v(4.9, -17.83) * mm, "end": v(5.4, -17.33) * mm});
            skLineSegment(sketch, "E361", {"start": v(31.54, -12.14) * mm, "end": v(31.32, -11.73) * mm});
            skLineSegment(sketch, "E362", {"start": v(33.28, -9.12) * mm, "end": v(33.68, -8.23) * mm});
            skLineSegment(sketch, "E363", {"start": v(31.84, -9.08) * mm, "end": v(32.82, -9.14) * mm});
            skLineSegment(sketch, "E364", {"start": v(28.05, -11.98) * mm, "end": v(28.12, -11.93) * mm});
            skLineSegment(sketch, "E365", {"start": v(-3.5, 2.21) * mm, "end": v(-3.64, 0) * mm});
            skLineSegment(sketch, "E366", {"start": v(-3.64, 0) * mm, "end": v(-3.5, -2.21) * mm});
            skLineSegment(sketch, "E367", {"start": v(-3.5, -2.21) * mm, "end": v(-3.09, -4.39) * mm});
            skLineSegment(sketch, "E368", {"start": v(31.15, -8.96) * mm, "end": v(31.84, -9.08) * mm});
            skLineSegment(sketch, "E369", {"start": v(-3.09, -4.39) * mm, "end": v(-2.4, -6.5) * mm});
            skLineSegment(sketch, "E370", {"start": v(32.82, -9.14) * mm, "end": v(33.28, -9.12) * mm});
            skLineSegment(sketch, "E371", {"start": v(-2.4, -6.5) * mm, "end": v(-1.46, -8.5) * mm});
            skLineSegment(sketch, "E372", {"start": v(-0.27, -10.37) * mm, "end": v(1.14, -12.08) * mm});
            skLineSegment(sketch, "E373", {"start": v(1.14, -12.08) * mm, "end": v(2.75, -13.6) * mm});
            skLineSegment(sketch, "E374", {"start": v(31.32, -11.73) * mm, "end": v(30.78, -10.9) * mm});
            skLineSegment(sketch, "E375", {"start": v(15.1, -17.6) * mm, "end": v(17.3, -17.33) * mm});
            skLineSegment(sketch, "E376", {"start": v(21.5, -15.96) * mm, "end": v(23.45, -14.9) * mm});
            skLineSegment(sketch, "E377", {"start": v(8.55, -16.78) * mm, "end": v(10.7, -17.33) * mm});
            skLineSegment(sketch, "E378", {"start": v(10.7, -17.33) * mm, "end": v(12.9, -17.6) * mm});
            skLineSegment(sketch, "E379", {"start": v(-1.46, 8.5) * mm, "end": v(-2.4, 6.5) * mm});
            skLineSegment(sketch, "E380", {"start": v(19.45, -16.78) * mm, "end": v(21.5, -15.96) * mm});
            skLineSegment(sketch, "E381", {"start": v(12.9, -17.6) * mm, "end": v(15.1, -17.6) * mm});
            skLineSegment(sketch, "E382", {"start": v(2.75, 13.6) * mm, "end": v(1.14, 12.08) * mm});
            skLineSegment(sketch, "E383", {"start": v(29.46, -8.5) * mm, "end": v(30.4, -6.5) * mm});
            skLineSegment(sketch, "E384", {"start": v(4.55, 14.9) * mm, "end": v(2.75, 13.6) * mm});
            skLineSegment(sketch, "E385", {"start": v(21.5, 15.96) * mm, "end": v(19.45, 16.78) * mm});
            skLineSegment(sketch, "E386", {"start": v(26.86, -12.08) * mm, "end": v(28.27, -10.37) * mm});
            skLineSegment(sketch, "E387", {"start": v(6.49, 15.96) * mm, "end": v(4.55, 14.9) * mm});
            skLineSegment(sketch, "E388", {"start": v(6.49, -15.96) * mm, "end": v(8.55, -16.78) * mm});
            skLineSegment(sketch, "E389", {"start": v(23.45, 14.9) * mm, "end": v(21.5, 15.96) * mm});
            skLineSegment(sketch, "E390", {"start": v(25.24, -13.6) * mm, "end": v(26.86, -12.08) * mm});
            skLineSegment(sketch, "E391", {"start": v(28.27, -10.37) * mm, "end": v(29.46, -8.5) * mm});
            skLineSegment(sketch, "E392", {"start": v(-0.27, 10.37) * mm, "end": v(-1.46, 8.5) * mm});
            skLineSegment(sketch, "E393", {"start": v(1.14, 12.08) * mm, "end": v(-0.27, 10.37) * mm});
            skLineSegment(sketch, "E394", {"start": v(23.45, -14.9) * mm, "end": v(25.24, -13.6) * mm});
            skLineSegment(sketch, "E395", {"start": v(30.4, -6.5) * mm, "end": v(31.08, -4.39) * mm});
            skLineSegment(sketch, "E396", {"start": v(17.3, -17.33) * mm, "end": v(19.45, -16.78) * mm});
            skLineSegment(sketch, "E397", {"start": v(-2.4, 6.5) * mm, "end": v(-3.09, 4.39) * mm});
            skLineSegment(sketch, "E398", {"start": v(31.5, 2.21) * mm, "end": v(31.08, 4.39) * mm});
            skLineSegment(sketch, "E399", {"start": v(31.08, -4.39) * mm, "end": v(31.5, -2.21) * mm});
            skLineSegment(sketch, "E400", {"start": v(29.46, 8.5) * mm, "end": v(28.27, 10.37) * mm});
            skLineSegment(sketch, "E401", {"start": v(26.86, 12.08) * mm, "end": v(25.24, 13.6) * mm});
            skLineSegment(sketch, "E402", {"start": v(31.08, 4.39) * mm, "end": v(30.4, 6.5) * mm});
            skLineSegment(sketch, "E403", {"start": v(31.5, -2.21) * mm, "end": v(31.64, 0) * mm});
            skLineSegment(sketch, "E404", {"start": v(31.64, 0) * mm, "end": v(31.5, 2.21) * mm});
            skLineSegment(sketch, "E405", {"start": v(28.27, 10.37) * mm, "end": v(26.86, 12.08) * mm});
            skLineSegment(sketch, "E406", {"start": v(30.4, 6.5) * mm, "end": v(29.46, 8.5) * mm});
            skLineSegment(sketch, "E407", {"start": v(25.24, 13.6) * mm, "end": v(23.45, 14.9) * mm});
            skLineSegment(sketch, "E408", {"start": v(13.33, 18.55) * mm, "end": v(13.41, 18.48) * mm});
            skLineSegment(sketch, "E409", {"start": v(27.4, 13) * mm, "end": v(27.34, 12.9) * mm});
            skLineSegment(sketch, "E410", {"start": v(27.58, 13.2) * mm, "end": v(27.4, 13) * mm});
            skLineSegment(sketch, "E411", {"start": v(27.9, 16.18) * mm, "end": v(27.47, 16) * mm});
            skLineSegment(sketch, "E412", {"start": v(27.82, 13.54) * mm, "end": v(28.15, 14.16) * mm});
            skLineSegment(sketch, "E413", {"start": v(28.64, 15.52) * mm, "end": v(27.9, 16.18) * mm});
            skLineSegment(sketch, "E414", {"start": v(28.15, 14.16) * mm, "end": v(28.5, 15.07) * mm});
            skLineSegment(sketch, "E415", {"start": v(28.5, 15.07) * mm, "end": v(28.64, 15.52) * mm});
            skLineSegment(sketch, "E416", {"start": v(27.34, 12.9) * mm, "end": v(27.34, 12.8) * mm});
            skLineSegment(sketch, "E417", {"start": v(30.4, 8.7) * mm, "end": v(30.3, 8.73) * mm});
            skLineSegment(sketch, "E418", {"start": v(17.22, 19.08) * mm, "end": v(17.12, 19.77) * mm});
            skLineSegment(sketch, "E419", {"start": v(29.73, 9.85) * mm, "end": v(29.8, 9.93) * mm});
            skLineSegment(sketch, "E420", {"start": v(30.22, 8.8) * mm, "end": v(29.74, 9.64) * mm});
            skLineSegment(sketch, "E421", {"start": v(30.3, 8.73) * mm, "end": v(30.22, 8.8) * mm});
            skLineSegment(sketch, "E422", {"start": v(0.1, -16.18) * mm, "end": v(0.52, -16) * mm});
            skLineSegment(sketch, "E423", {"start": v(1.4, 15.55) * mm, "end": v(0.52, 16) * mm});
            skLineSegment(sketch, "E424", {"start": v(31.52, 6.43) * mm, "end": v(31.77, 6.53) * mm});
            skLineSegment(sketch, "E425", {"start": v(31.43, 6.37) * mm, "end": v(31.52, 6.43) * mm});
            skLineSegment(sketch, "E426", {"start": v(32.13, 6.75) * mm, "end": v(32.68, 7.18) * mm});
            skLineSegment(sketch, "E427", {"start": v(30.74, 8.84) * mm, "end": v(30.5, 8.72) * mm});
            skLineSegment(sketch, "E428", {"start": v(33.28, 9.12) * mm, "end": v(32.82, 9.14) * mm});
            skLineSegment(sketch, "E429", {"start": v(30.78, 10.9) * mm, "end": v(31.32, 11.73) * mm});
            skLineSegment(sketch, "E430", {"start": v(24.54, -15.73) * mm, "end": v(24.4, -15.5) * mm});
            skLineSegment(sketch, "E431", {"start": v(6.88, 18) * mm, "end": v(6.96, 17.58) * mm});
            skLineSegment(sketch, "E432", {"start": v(24.7, -16.12) * mm, "end": v(24.54, -15.73) * mm});
            skLineSegment(sketch, "E433", {"start": v(-3.53, -6.43) * mm, "end": v(-3.77, -6.53) * mm});
            skLineSegment(sketch, "E434", {"start": v(18.82, -18.74) * mm, "end": v(19.19, -19.33) * mm});
            skLineSegment(sketch, "E435", {"start": v(33.38, 7.87) * mm, "end": v(33.68, 8.23) * mm});
            skLineSegment(sketch, "E436", {"start": v(32.68, 7.18) * mm, "end": v(33.38, 7.87) * mm});
            skLineSegment(sketch, "E437", {"start": v(6.83, 18.69) * mm, "end": v(6.88, 18) * mm});
            skLineSegment(sketch, "E438", {"start": v(5.4, 17.33) * mm, "end": v(4.9, 17.83) * mm});
            skLineSegment(sketch, "E439", {"start": v(29.7, 9.75) * mm, "end": v(29.73, 9.85) * mm});
            skLineSegment(sketch, "E440", {"start": v(31.77, 6.53) * mm, "end": v(32.13, 6.75) * mm});
            skLineSegment(sketch, "E441", {"start": v(21.12, -19.67) * mm, "end": v(21.17, -18.69) * mm});
            skLineSegment(sketch, "E442", {"start": v(24.36, -15.4) * mm, "end": v(24.38, -15.3) * mm});
            skLineSegment(sketch, "E443", {"start": v(5.4, -17.33) * mm, "end": v(5.65, -17) * mm});
            skLineSegment(sketch, "E444", {"start": v(0.52, -16) * mm, "end": v(1.4, -15.55) * mm});
            skLineSegment(sketch, "E445", {"start": v(22.22, -16.76) * mm, "end": v(22.35, -17) * mm});
            skLineSegment(sketch, "E446", {"start": v(-5.77, -3.14) * mm, "end": v(-6.6, -3.67) * mm});
            skLineSegment(sketch, "E447", {"start": v(9.44, -18.1) * mm, "end": v(9.49, -18) * mm});
            skLineSegment(sketch, "E448", {"start": v(31.84, 9.08) * mm, "end": v(31.15, 8.96) * mm});
            skLineSegment(sketch, "E449", {"start": v(33.68, 8.23) * mm, "end": v(33.28, 9.12) * mm});
            skLineSegment(sketch, "E450", {"start": v(34.96, -3.95) * mm, "end": v(34.6, -3.67) * mm});
            skLineSegment(sketch, "E451", {"start": v(21.06, -20.13) * mm, "end": v(21.12, -19.67) * mm});
            skLineSegment(sketch, "E452", {"start": v(31.15, 8.96) * mm, "end": v(30.74, 8.84) * mm});
            skLineSegment(sketch, "E453", {"start": v(2.56, 14.62) * mm, "end": v(2.47, 14.68) * mm});
            skLineSegment(sketch, "E454", {"start": v(5.84, -16.67) * mm, "end": v(5.95, -16.64) * mm});
            skLineSegment(sketch, "E455", {"start": v(32.82, 9.14) * mm, "end": v(31.84, 9.08) * mm});
            skLineSegment(sketch, "E456", {"start": v(0.66, -12.9) * mm, "end": v(0.6, -13) * mm});
            skLineSegment(sketch, "E457", {"start": v(0.66, -12.8) * mm, "end": v(0.66, -12.9) * mm});
            skLineSegment(sketch, "E458", {"start": v(29.8, 9.93) * mm, "end": v(30.02, 10.08) * mm});
            skLineSegment(sketch, "E459", {"start": v(2.56, -14.62) * mm, "end": v(2.66, -14.6) * mm});
            skLineSegment(sketch, "E460", {"start": v(2.3, -14.88) * mm, "end": v(2.47, -14.68) * mm});
            skLineSegment(sketch, "E461", {"start": v(9.18, -18.74) * mm, "end": v(9.36, -18.36) * mm});
            skLineSegment(sketch, "E462", {"start": v(8.2, -20.1) * mm, "end": v(8.81, -19.33) * mm});
            skLineSegment(sketch, "E463", {"start": v(8.81, -19.33) * mm, "end": v(9.18, -18.74) * mm});
            skLineSegment(sketch, "E464", {"start": v(1.4, -15.55) * mm, "end": v(1.98, -15.16) * mm});
            skLineSegment(sketch, "E465", {"start": v(2.47, -14.68) * mm, "end": v(2.56, -14.62) * mm});
            skLineSegment(sketch, "E466", {"start": v(7.88, -20.44) * mm, "end": v(8.2, -20.1) * mm});
            skLineSegment(sketch, "E467", {"start": v(1.98, -15.16) * mm, "end": v(2.3, -14.88) * mm});
            skLineSegment(sketch, "E468", {"start": v(0.42, -13.2) * mm, "end": v(0.18, -13.54) * mm});
            skLineSegment(sketch, "E469", {"start": v(0.6, -13) * mm, "end": v(0.42, -13.2) * mm});
            skLineSegment(sketch, "E470", {"start": v(2.76, -14.64) * mm, "end": v(3.54, -15.21) * mm});
            skLineSegment(sketch, "E471", {"start": v(-1.56, 12.6) * mm, "end": v(-2.5, 12.85) * mm});
            skLineSegment(sketch, "E472", {"start": v(-6.96, -3.95) * mm, "end": v(-6.76, -4.92) * mm});
            skLineSegment(sketch, "E473", {"start": v(-0.91, 12.33) * mm, "end": v(-1.56, 12.6) * mm});
            skLineSegment(sketch, "E474", {"start": v(-0.54, 12.12) * mm, "end": v(-0.91, 12.33) * mm});
            skLineSegment(sketch, "E475", {"start": v(29.56, -12.6) * mm, "end": v(30.5, -12.85) * mm});
            skLineSegment(sketch, "E476", {"start": v(30.02, 10.08) * mm, "end": v(30.33, 10.37) * mm});
            skLineSegment(sketch, "E477", {"start": v(-6.6, -3.67) * mm, "end": v(-6.96, -3.95) * mm});
            skLineSegment(sketch, "E478", {"start": v(31.77, -6.53) * mm, "end": v(31.52, -6.43) * mm});
            skLineSegment(sketch, "E479", {"start": v(-0.33, 11.96) * mm, "end": v(-0.54, 12.12) * mm});
            skLineSegment(sketch, "E480", {"start": v(30.33, 10.37) * mm, "end": v(30.78, 10.9) * mm});
            skLineSegment(sketch, "E481", {"start": v(30.96, 12.93) * mm, "end": v(30.5, 12.85) * mm});
            skLineSegment(sketch, "E482", {"start": v(28.15, -14.16) * mm, "end": v(27.82, -13.54) * mm});
            skLineSegment(sketch, "E483", {"start": v(-0.15, -14.16) * mm, "end": v(-0.5, -15.07) * mm});
            skLineSegment(sketch, "E484", {"start": v(14.7, -18.65) * mm, "end": v(14.72, -18.92) * mm});
            skLineSegment(sketch, "E485", {"start": v(0.18, -13.54) * mm, "end": v(-0.15, -14.16) * mm});
            skLineSegment(sketch, "E486", {"start": v(3.61, -15.3) * mm, "end": v(3.64, -15.4) * mm});
            skLineSegment(sketch, "E487", {"start": v(27.82, -13.54) * mm, "end": v(27.58, -13.2) * mm});
            skLineSegment(sketch, "E488", {"start": v(12.95, -19.99) * mm, "end": v(13.18, -19.33) * mm});
            skLineSegment(sketch, "E489", {"start": v(31.54, 12.14) * mm, "end": v(30.96, 12.93) * mm});
            skLineSegment(sketch, "E490", {"start": v(14.72, -18.92) * mm, "end": v(14.81, -19.33) * mm});
            skLineSegment(sketch, "E491", {"start": v(28.5, -15.07) * mm, "end": v(28.15, -14.16) * mm});
            skLineSegment(sketch, "E492", {"start": v(30.78, -10.9) * mm, "end": v(30.33, -10.37) * mm});
            skLineSegment(sketch, "E493", {"start": v(31.32, 11.73) * mm, "end": v(31.54, 12.14) * mm});
            skLineSegment(sketch, "E494", {"start": v(31.4, -6.16) * mm, "end": v(31.7, -5.24) * mm});
            skLineSegment(sketch, "E495", {"start": v(17.12, -19.77) * mm, "end": v(17.22, -19.08) * mm});
            skLineSegment(sketch, "E496", {"start": v(29.56, 12.6) * mm, "end": v(28.9, 12.33) * mm});
            skLineSegment(sketch, "E497", {"start": v(28.12, 11.93) * mm, "end": v(28.03, 11.99) * mm});
            skLineSegment(sketch, "E498", {"start": v(14.67, -18.55) * mm, "end": v(14.7, -18.65) * mm});
            skLineSegment(sketch, "E499", {"start": v(13.52, -18.45) * mm, "end": v(14.48, -18.45) * mm});
            skLineSegment(sketch, "E500", {"start": v(28.54, 12.12) * mm, "end": v(28.33, 11.96) * mm});
            skLineSegment(sketch, "E501", {"start": v(28.33, 11.96) * mm, "end": v(28.23, 11.92) * mm});
            skLineSegment(sketch, "E502", {"start": v(16.87, -20.72) * mm, "end": v(17.12, -19.77) * mm});
            skLineSegment(sketch, "E503", {"start": v(28.9, 12.33) * mm, "end": v(28.54, 12.12) * mm});
            skLineSegment(sketch, "E504", {"start": v(17.22, -19.08) * mm, "end": v(17.23, -18.66) * mm});
            skLineSegment(sketch, "E505", {"start": v(28.23, 11.92) * mm, "end": v(28.12, 11.93) * mm});
            skLineSegment(sketch, "E506", {"start": v(16.72, -21.16) * mm, "end": v(16.87, -20.72) * mm});
            skLineSegment(sketch, "E507", {"start": v(30.5, 12.85) * mm, "end": v(29.56, 12.6) * mm});
            skLineSegment(sketch, "E508", {"start": v(29.56, -12.6) * mm, "end": v(28.9, -12.33) * mm});
            skLineSegment(sketch, "E509", {"start": v(31.43, -6.37) * mm, "end": v(31.52, -6.43) * mm});
            skLineSegment(sketch, "E510", {"start": v(31.15, -8.96) * mm, "end": v(30.74, -8.84) * mm});
            skLineSegment(sketch, "E511", {"start": v(30.74, -8.84) * mm, "end": v(30.5, -8.72) * mm});
            skLineSegment(sketch, "E512", {"start": v(32.44, -1.35) * mm, "end": v(32.4, -1.43) * mm});
            skLineSegment(sketch, "E513", {"start": v(34.76, -4.92) * mm, "end": v(34.3, -5.02) * mm});
            skLineSegment(sketch, "E514", {"start": v(35.33, -0.5) * mm, "end": v(34.9, -0.7) * mm});
            skLineSegment(sketch, "E515", {"start": v(33.14, -2.83) * mm, "end": v(33.77, -3.14) * mm});
            skLineSegment(sketch, "E516", {"start": v(32.74, -2.7) * mm, "end": v(33.14, -2.83) * mm});
            skLineSegment(sketch, "E517", {"start": v(33.77, -3.14) * mm, "end": v(34.6, -3.67) * mm});
            skLineSegment(sketch, "E518", {"start": v(32.62, -1.25) * mm, "end": v(32.52, -1.28) * mm});
            skLineSegment(sketch, "E519", {"start": v(33.99, -1.04) * mm, "end": v(33.3, -1.2) * mm});
            skLineSegment(sketch, "E520", {"start": v(35.33, 0.5) * mm, "end": v(35.33, -0.5) * mm});
            skLineSegment(sketch, "E521", {"start": v(34.9, 0.7) * mm, "end": v(35.33, 0.5) * mm});
            skLineSegment(sketch, "E522", {"start": v(32.38, -2.6) * mm, "end": v(32.48, -2.65) * mm});
            skLineSegment(sketch, "E523", {"start": v(32.62, 1.25) * mm, "end": v(32.9, 1.26) * mm});
            skLineSegment(sketch, "E524", {"start": v(33.3, -1.2) * mm, "end": v(32.9, -1.26) * mm});
            skLineSegment(sketch, "E525", {"start": v(32.31, -2.53) * mm, "end": v(32.38, -2.6) * mm});
            skLineSegment(sketch, "E526", {"start": v(32.52, 1.28) * mm, "end": v(32.62, 1.25) * mm});
            skLineSegment(sketch, "E527", {"start": v(32.9, -1.26) * mm, "end": v(32.62, -1.25) * mm});
            skLineSegment(sketch, "E528", {"start": v(32.48, -2.65) * mm, "end": v(32.74, -2.7) * mm});
            skLineSegment(sketch, "E529", {"start": v(32.44, 1.35) * mm, "end": v(32.52, 1.28) * mm});
            skLineSegment(sketch, "E530", {"start": v(32.4, 1.43) * mm, "end": v(32.44, 1.35) * mm});
            skLineSegment(sketch, "E531", {"start": v(32.9, 1.26) * mm, "end": v(33.3, 1.2) * mm});
            skLineSegment(sketch, "E532", {"start": v(33.3, 1.2) * mm, "end": v(33.99, 1.04) * mm});
            skLineSegment(sketch, "E533", {"start": v(33.99, 1.04) * mm, "end": v(34.9, 0.7) * mm});
            skLineSegment(sketch, "E534", {"start": v(32.52, -1.28) * mm, "end": v(32.44, -1.35) * mm});
            skLineSegment(sketch, "E535", {"start": v(34.9, -0.7) * mm, "end": v(33.99, -1.04) * mm});
            skLineSegment(sketch, "E536", {"start": v(31.4, 6.16) * mm, "end": v(31.7, 5.24) * mm});
            skLineSegment(sketch, "E537", {"start": v(31.75, 5.15) * mm, "end": v(31.85, 5.1) * mm});
            skLineSegment(sketch, "E538", {"start": v(32.22, -5.16) * mm, "end": v(31.96, -5.1) * mm});
            skLineSegment(sketch, "E539", {"start": v(33.14, 2.83) * mm, "end": v(32.74, 2.7) * mm});
            skLineSegment(sketch, "E540", {"start": v(32.38, 2.6) * mm, "end": v(32.31, 2.52) * mm});
            skLineSegment(sketch, "E541", {"start": v(32.74, 2.7) * mm, "end": v(32.48, 2.65) * mm});
            skLineSegment(sketch, "E542", {"start": v(32.48, 2.65) * mm, "end": v(32.38, 2.6) * mm});
            skLineSegment(sketch, "E543", {"start": v(34.3, 5.02) * mm, "end": v(34.76, 4.92) * mm});
            skLineSegment(sketch, "E544", {"start": v(31.43, 6.37) * mm, "end": v(31.39, 6.27) * mm});
            skLineSegment(sketch, "E545", {"start": v(34.76, 4.92) * mm, "end": v(34.96, 3.95) * mm});
            skLineSegment(sketch, "E546", {"start": v(31.96, 5.1) * mm, "end": v(32.22, 5.16) * mm});
            skLineSegment(sketch, "E547", {"start": v(33.77, 3.14) * mm, "end": v(33.14, 2.83) * mm});
            skLineSegment(sketch, "E548", {"start": v(32.22, 5.16) * mm, "end": v(32.63, 5.2) * mm});
            skLineSegment(sketch, "E549", {"start": v(33.33, 5.17) * mm, "end": v(34.3, 5.02) * mm});
            skLineSegment(sketch, "E550", {"start": v(32.3, 2.4) * mm, "end": v(32.31, 2.52) * mm});
            skLineSegment(sketch, "E551", {"start": v(32.3, -2.4) * mm, "end": v(32.31, -2.53) * mm});
            skLineSegment(sketch, "E552", {"start": v(32.63, 5.2) * mm, "end": v(33.33, 5.17) * mm});
            skLineSegment(sketch, "E553", {"start": v(5.77, 16.76) * mm, "end": v(5.65, 17) * mm});
            skLineSegment(sketch, "E554", {"start": v(-0.64, 15.52) * mm, "end": v(0.1, 16.18) * mm});
            skLineSegment(sketch, "E555", {"start": v(-3.4, -6.27) * mm, "end": v(-3.44, -6.37) * mm});
            skLineSegment(sketch, "E556", {"start": v(25.09, -18.22) * mm, "end": v(24.24, -18.72) * mm});
            skLineSegment(sketch, "E557", {"start": v(10.78, -19.08) * mm, "end": v(10.77, -18.66) * mm});
            skLineSegment(sketch, "E558", {"start": v(-1.56, -12.6) * mm, "end": v(-2.5, -12.85) * mm});
            skLineSegment(sketch, "E559", {"start": v(18.64, -18.36) * mm, "end": v(18.82, -18.74) * mm});
            skLineSegment(sketch, "E560", {"start": v(27.34, -12.8) * mm, "end": v(27.34, -12.9) * mm});
            skLineSegment(sketch, "E561", {"start": v(-3.53, -6.43) * mm, "end": v(-3.44, -6.37) * mm});
            skLineSegment(sketch, "E562", {"start": v(-2.5, -12.85) * mm, "end": v(-2.97, -12.93) * mm});
            skLineSegment(sketch, "E563", {"start": v(-0.64, -15.52) * mm, "end": v(-0.5, -15.07) * mm});
            skLineSegment(sketch, "E564", {"start": v(-0.91, -12.33) * mm, "end": v(-1.56, -12.6) * mm});
            skLineSegment(sketch, "E565", {"start": v(21.06, -20.13) * mm, "end": v(20.12, -20.44) * mm});
            skLineSegment(sketch, "E566", {"start": v(30.02, -10.08) * mm, "end": v(30.33, -10.37) * mm});
            skLineSegment(sketch, "E567", {"start": v(0.1, -16.18) * mm, "end": v(-0.64, -15.52) * mm});
            skLineSegment(sketch, "E568", {"start": v(14.81, -19.33) * mm, "end": v(15.05, -19.99) * mm});
            skLineSegment(sketch, "E569", {"start": v(-0.54, -12.12) * mm, "end": v(-0.91, -12.33) * mm});
            skLineSegment(sketch, "E570", {"start": v(-0.33, -11.96) * mm, "end": v(-0.54, -12.12) * mm});
            skLineSegment(sketch, "E571", {"start": v(-1.73, -9.85) * mm, "end": v(-1.8, -9.93) * mm});
            skLineSegment(sketch, "E572", {"start": v(31.54, -12.14) * mm, "end": v(30.96, -12.93) * mm});
            skLineSegment(sketch, "E573", {"start": v(-1.7, -9.75) * mm, "end": v(-1.73, -9.85) * mm});
            skLineSegment(sketch, "E574", {"start": v(-1.74, -9.64) * mm, "end": v(-1.7, -9.75) * mm});
            skLineSegment(sketch, "E575", {"start": v(9.58, -17.95) * mm, "end": v(9.49, -18) * mm});
            skLineSegment(sketch, "E576", {"start": v(19.8, -20.1) * mm, "end": v(19.19, -19.33) * mm});
            skLineSegment(sketch, "E577", {"start": v(29.8, -9.93) * mm, "end": v(30.02, -10.08) * mm});
            skLineSegment(sketch, "E578", {"start": v(29.73, -9.85) * mm, "end": v(29.8, -9.93) * mm});
            skLineSegment(sketch, "E579", {"start": v(30.96, -12.93) * mm, "end": v(30.5, -12.85) * mm});
            skLineSegment(sketch, "E580", {"start": v(-0.23, -11.92) * mm, "end": v(-0.33, -11.96) * mm});
            skLineSegment(sketch, "E581", {"start": v(29.7, -9.75) * mm, "end": v(29.73, -9.85) * mm});
            skLineSegment(sketch, "E582", {"start": v(-5.3, 1.2) * mm, "end": v(-4.9, 1.26) * mm});
            skLineSegment(sketch, "E583", {"start": v(25.7, -14.88) * mm, "end": v(25.53, -14.68) * mm});
            skLineSegment(sketch, "E584", {"start": v(25.53, -14.68) * mm, "end": v(25.44, -14.62) * mm});
            skLineSegment(sketch, "E585", {"start": v(-4.13, -6.75) * mm, "end": v(-3.77, -6.53) * mm});
            skLineSegment(sketch, "E586", {"start": v(-0.12, -11.93) * mm, "end": v(-0.23, -11.92) * mm});
            skLineSegment(sketch, "E587", {"start": v(24.9, -16.8) * mm, "end": v(25.05, -17.76) * mm});
            skLineSegment(sketch, "E588", {"start": v(25.44, -14.62) * mm, "end": v(25.33, -14.6) * mm});
            skLineSegment(sketch, "E589", {"start": v(-4.44, -1.35) * mm, "end": v(-4.4, -1.45) * mm});
            skLineSegment(sketch, "E590", {"start": v(-4.69, -7.18) * mm, "end": v(-4.13, -6.75) * mm});
            skLineSegment(sketch, "E591", {"start": v(-3.32, -11.73) * mm, "end": v(-2.78, -10.9) * mm});
            skLineSegment(sketch, "E592", {"start": v(25.23, -14.64) * mm, "end": v(24.46, -15.21) * mm});
            skLineSegment(sketch, "E593", {"start": v(-0.12, 11.93) * mm, "end": v(0.51, 12.66) * mm});
            skLineSegment(sketch, "E594", {"start": v(-1.7, -9.75) * mm, "end": v(-2.21, -8.9) * mm});
            skLineSegment(sketch, "E595", {"start": v(-4.44, 1.35) * mm, "end": v(-4.35, 2.32) * mm});
            skLineSegment(sketch, "E596", {"start": v(28.12, 11.93) * mm, "end": v(27.48, 12.66) * mm});
            skLineSegment(sketch, "E597", {"start": v(9.64, 17.95) * mm, "end": v(9.7, 17.95) * mm});
            skLineSegment(sketch, "E598", {"start": v(9.7, 17.95) * mm, "end": v(10.18, 18.1) * mm});
            skLineSegment(sketch, "E599", {"start": v(32.4, 1.43) * mm, "end": v(32.35, 1.9) * mm});
            skLineSegment(sketch, "E600", {"start": v(32.35, 1.9) * mm, "end": v(32.37, 1.98) * mm});
            skLineSegment(sketch, "E601", {"start": v(9.64, -17.95) * mm, "end": v(9.7, -17.95) * mm});
            skLineSegment(sketch, "E602", {"start": v(9.7, -17.95) * mm, "end": v(10.18, -18.1) * mm});
            skLineSegment(sketch, "E603", {"start": v(32.37, -1.98) * mm, "end": v(32.35, -1.9) * mm});
            skLineSegment(sketch, "E604", {"start": v(32.35, -1.9) * mm, "end": v(32.4, -1.43) * mm});
            skLineSegment(sketch, "E605", {"start": v(-0.04, -11.99) * mm, "end": v(0.56, -12.65) * mm});
            skLineSegment(sketch, "E606", {"start": v(0.56, -12.65) * mm, "end": v(0.6, -12.7) * mm});
            skLineSegment(sketch, "E607", {"start": v(10.63, -18.15) * mm, "end": v(10.58, -18.14) * mm});
            skLineSegment(sketch, "E608", {"start": v(10.58, -18.14) * mm, "end": v(9.7, -17.95) * mm});
            skLineSegment(sketch, "E609", {"start": v(21.02, -17.09) * mm, "end": v(20.98, -17.12) * mm});
            skLineSegment(sketch, "E610", {"start": v(17.47, 18.17) * mm, "end": v(17.37, 18.18) * mm});
            skLineSegment(sketch, "E611", {"start": v(32.35, -2.27) * mm, "end": v(32.35, -2.32) * mm});
            skLineSegment(sketch, "E612", {"start": v(9.64, -17.95) * mm, "end": v(9.58, -17.95) * mm});
            skLineSegment(sketch, "E613", {"start": v(32.33, 2.41) * mm, "end": v(32.35, 2.32) * mm});
            skLineSegment(sketch, "E614", {"start": v(32.34, -2.06) * mm, "end": v(32.35, -1.9) * mm});
            skLineSegment(sketch, "E615", {"start": v(9.7, 17.95) * mm, "end": v(10.58, 18.14) * mm});
            skLineSegment(sketch, "E616", {"start": v(10.58, 18.14) * mm, "end": v(10.63, 18.15) * mm});
            skLineSegment(sketch, "E617", {"start": v(27.39, 12.7) * mm, "end": v(27.51, 12.57) * mm});
            skLineSegment(sketch, "E618", {"start": v(27.51, 12.57) * mm, "end": v(28.03, 11.99) * mm});
            skLineSegment(sketch, "E619", {"start": v(21.02, 17.09) * mm, "end": v(20.98, 17.12) * mm});
            skLineSegment(sketch, "E620", {"start": v(9.64, 17.95) * mm, "end": v(9.58, 17.95) * mm});
            skLineSegment(sketch, "E621", {"start": v(-4.4, -1.45) * mm, "end": v(-4.36, -1.9) * mm});
            skLineSegment(sketch, "E622", {"start": v(-4.36, -1.9) * mm, "end": v(-4.3, -2.4) * mm});
            skLineSegment(sketch, "E623", {"start": v(0.6, 12.7) * mm, "end": v(0.56, 12.65) * mm});
            skLineSegment(sketch, "E624", {"start": v(0.56, 12.65) * mm, "end": v(-0.04, 11.99) * mm});
            skLineSegment(sketch, "E625", {"start": v(-1.74, 9.64) * mm, "end": v(-2.17, 8.9) * mm});
            skLineSegment(sketch, "E626", {"start": v(-2.17, 8.9) * mm, "end": v(-2.22, 8.8) * mm});
            skLineSegment(sketch, "E627", {"start": v(6.95, 17.06) * mm, "end": v(6.17, 16.71) * mm});
            skLineSegment(sketch, "E628", {"start": v(6.17, 16.71) * mm, "end": v(6.05, 16.66) * mm});
            skLineSegment(sketch, "E629", {"start": v(-2.22, -8.8) * mm, "end": v(-2.17, -8.9) * mm});
            skLineSegment(sketch, "E630", {"start": v(-2.17, -8.9) * mm, "end": v(-1.74, -9.64) * mm});
            skLineSegment(sketch, "E631", {"start": v(4.55, -14.9) * mm, "end": v(4.59, -14.92) * mm});
            skLineSegment(sketch, "E632", {"start": v(4.59, -14.92) * mm, "end": v(6.49, -15.96) * mm});
            skLineSegment(sketch, "E633", {"start": v(-1.46, -8.5) * mm, "end": v(-1.43, -8.54) * mm});
            skLineSegment(sketch, "E634", {"start": v(-1.43, -8.54) * mm, "end": v(-0.27, -10.37) * mm});
            skLineSegment(sketch, "E635", {"start": v(32.34, -2.06) * mm, "end": v(32.3, -2.4) * mm});
            skLineSegment(sketch, "E636", {"start": v(32.3, 2.4) * mm, "end": v(32.37, 1.98) * mm});
            skLineSegment(sketch, "E637", {"start": v(32.35, 2.32) * mm, "end": v(32.35, 2.27) * mm});
            skLineSegment(sketch, "E638", {"start": v(17.79, 18.09) * mm, "end": v(17.5, 18.12) * mm});
            skLineSegment(sketch, "E639", {"start": v(17.5, 18.12) * mm, "end": v(17.36, 18.15) * mm});
            skLineSegment(sketch, "E640", {"start": v(6.05, -16.66) * mm, "end": v(6.17, -16.71) * mm});
            skLineSegment(sketch, "E641", {"start": v(6.17, -16.71) * mm, "end": v(6.43, -16.86) * mm});
            skLineSegment(sketch, "E642", {"start": v(-4.3, 2.4) * mm, "end": v(-4.34, 2.06) * mm});
            skLineSegment(sketch, "E643", {"start": v(17.36, -18.15) * mm, "end": v(17.5, -18.12) * mm});
            skLineSegment(sketch, "E644", {"start": v(17.5, -18.12) * mm, "end": v(17.79, -18.09) * mm});
            skLineSegment(sketch, "E645", {"start": v(27.39, -12.7) * mm, "end": v(27.51, -12.57) * mm});
            skLineSegment(sketch, "E646", {"start": v(27.51, -12.57) * mm, "end": v(27.7, -12.4) * mm});
            skLineSegment(sketch, "E647", {"start": v(21.05, -17.07) * mm, "end": v(21.86, -16.75) * mm});
            skLineSegment(sketch, "E648", {"start": v(-2.3, 8.73) * mm, "end": v(-2.21, 8.9) * mm});
            skLineSegment(sketch, "E649", {"start": v(5.95, -16.64) * mm, "end": v(6.13, -16.74) * mm});
            skLineSegment(sketch, "E650", {"start": v(21.05, 17.07) * mm, "end": v(21.86, 16.75) * mm});
            skLineSegment(sketch, "E651", {"start": v(-2.21, -8.9) * mm, "end": v(-2.3, -8.73) * mm});
            skLineSegment(sketch, "E652", {"start": v(30.3, 8.73) * mm, "end": v(30.21, 8.9) * mm});
            skLineSegment(sketch, "E653", {"start": v(31.4, 6.16) * mm, "end": v(31.39, 6.27) * mm});
            skLineSegment(sketch, "E654", {"start": v(31.7, 5.24) * mm, "end": v(31.75, 5.15) * mm});
            skLineSegment(sketch, "E655", {"start": v(3.54, -15.21) * mm, "end": v(3.61, -15.3) * mm});
            skLineSegment(sketch, "E656", {"start": v(2.76, -14.64) * mm, "end": v(2.66, -14.6) * mm});
            skLineSegment(sketch, "E657", {"start": v(-3.75, -5.15) * mm, "end": v(-3.7, -5.24) * mm});
            skLineSegment(sketch, "E658", {"start": v(-3.4, -6.16) * mm, "end": v(-3.4, -6.27) * mm});
            skLineSegment(sketch, "E659", {"start": v(31.4, -6.16) * mm, "end": v(31.39, -6.27) * mm});
            skLineSegment(sketch, "E660", {"start": v(31.7, -5.24) * mm, "end": v(31.75, -5.15) * mm});
            skLineSegment(sketch, "E661", {"start": v(24.46, -15.21) * mm, "end": v(24.38, -15.3) * mm});
            skLineSegment(sketch, "E662", {"start": v(25.33, -14.6) * mm, "end": v(25.23, -14.64) * mm});
            skLineSegment(sketch, "E663", {"start": v(-3.4, 6.27) * mm, "end": v(-3.4, 6.16) * mm});
            skLineSegment(sketch, "E664", {"start": v(-3.7, 5.24) * mm, "end": v(-3.75, 5.15) * mm});
            skLineSegment(sketch, "E665", {"start": v(13.52, -18.45) * mm, "end": v(13.41, -18.48) * mm});
            skLineSegment(sketch, "E666", {"start": v(14.48, -18.45) * mm, "end": v(14.59, -18.48) * mm});
            skLineSegment(sketch, "E667", {"start": v(25.33, 14.6) * mm, "end": v(25.23, 14.64) * mm});
            skLineSegment(sketch, "E668", {"start": v(24.46, 15.21) * mm, "end": v(24.38, 15.3) * mm});
            skLineSegment(sketch, "E669", {"start": v(2.76, 14.64) * mm, "end": v(2.66, 14.6) * mm});
            skLineSegment(sketch, "E670", {"start": v(3.54, 15.21) * mm, "end": v(3.61, 15.3) * mm});
            skLineSegment(sketch, "E671", {"start": v(-4.34, 2.06) * mm, "end": v(-4.4, 1.45) * mm});
            skLineSegment(sketch, "E672", {"start": v(29.74, 9.64) * mm, "end": v(29.7, 9.75) * mm});
            skLineSegment(sketch, "E673", {"start": v(13.41, 18.48) * mm, "end": v(13.52, 18.45) * mm});
            skLineSegment(sketch, "E674", {"start": v(14.48, 18.45) * mm, "end": v(14.59, 18.48) * mm});
            skLineSegment(sketch, "E675", {"start": v(14, 1.75) * mm, "end": v(14, -1.75) * mm});
            skPoint(sketch, "E676", {"position": v(14, 0) * mm});
            skSolve(sketch);
        }
        {
            var Q0;
            Q0=makeQuery(id+"F0.imprint","IMPRINT",FACE,{"disambiguationData":[TD([[makeQuery(id+"F0.imprint","IMPRINT",EDGE,{"derivedFrom":sQuery(id+"F0.wireOp",EDGE,"E2")}),1.0]])]});
            var Q1;
            Q1=makeQuery(id+"F0.imprint","IMPRINT",FACE,{"disambiguationData":[TD([[makeQuery(id+"F0.imprint","IMPRINT",EDGE,{"derivedFrom":sQuery(id+"F0.wireOp",EDGE,"E110")}),1.0]])]});
            extrude(context, id + "F1", {"entities" : qUnion([Q0, Q1]), "depth" : 5.4 * mm, "offsetDistance" : 25 * mm});
        }
        {
            var Q0;
            Q0=makeQuery(id+"F1.opExtrude","CAP_FACE",FACE,{"disambiguationData":[OSD([sQuery(id+"F0.wireOp",EDGE,"E2"),sQuery(id+"F0.wireOp",EDGE,"E8"),sQuery(id+"F0.wireOp",EDGE,"E10"),sQuery(id+"F0.wireOp",EDGE,"E21"),sQuery(id+"F0.wireOp",EDGE,"E22"),sQuery(id+"F0.wireOp",EDGE,"E27"),sQuery(id+"F0.wireOp",EDGE,"E28"),sQuery(id+"F0.wireOp",EDGE,"E29"),sQuery(id+"F0.wireOp",EDGE,"E30"),sQuery(id+"F0.wireOp",EDGE,"E31"),sQuery(id+"F0.wireOp",EDGE,"E32"),sQuery(id+"F0.wireOp",EDGE,"E33"),sQuery(id+"F0.wireOp",EDGE,"E34"),sQuery(id+"F0.wireOp",EDGE,"E35"),sQuery(id+"F0.wireOp",EDGE,"E36"),sQuery(id+"F0.wireOp",EDGE,"E37"),sQuery(id+"F0.wireOp",EDGE,"E38"),sQuery(id+"F0.wireOp",EDGE,"E39"),sQuery(id+"F0.wireOp",EDGE,"E40"),sQuery(id+"F0.wireOp",EDGE,"E41"),sQuery(id+"F0.wireOp",EDGE,"E42"),sQuery(id+"F0.wireOp",EDGE,"E43"),sQuery(id+"F0.wireOp",EDGE,"E44"),sQuery(id+"F0.wireOp",EDGE,"E45"),sQuery(id+"F0.wireOp",EDGE,"E46"),sQuery(id+"F0.wireOp",EDGE,"E47"),sQuery(id+"F0.wireOp",EDGE,"E48"),sQuery(id+"F0.wireOp",EDGE,"E49"),sQuery(id+"F0.wireOp",EDGE,"E50"),sQuery(id+"F0.wireOp",EDGE,"E51"),sQuery(id+"F0.wireOp",EDGE,"E52"),sQuery(id+"F0.wireOp",EDGE,"E53"),sQuery(id+"F0.wireOp",EDGE,"E54"),sQuery(id+"F0.wireOp",EDGE,"E55"),sQuery(id+"F0.wireOp",EDGE,"E56"),sQuery(id+"F0.wireOp",EDGE,"E57"),sQuery(id+"F0.wireOp",EDGE,"E58"),sQuery(id+"F0.wireOp",EDGE,"E59"),sQuery(id+"F0.wireOp",EDGE,"E60"),sQuery(id+"F0.wireOp",EDGE,"E61"),sQuery(id+"F0.wireOp",EDGE,"E62"),sQuery(id+"F0.wireOp",EDGE,"E63"),sQuery(id+"F0.wireOp",EDGE,"E64"),sQuery(id+"F0.wireOp",EDGE,"E65"),sQuery(id+"F0.wireOp",EDGE,"E66"),sQuery(id+"F0.wireOp",EDGE,"E83"),sQuery(id+"F0.wireOp",EDGE,"E84"),sQuery(id+"F0.wireOp",EDGE,"E85"),sQuery(id+"F0.wireOp",EDGE,"E86"),sQuery(id+"F0.wireOp",EDGE,"E87"),sQuery(id+"F0.wireOp",EDGE,"E88"),sQuery(id+"F0.wireOp",EDGE,"E89"),sQuery(id+"F0.wireOp",EDGE,"E90"),sQuery(id+"F0.wireOp",EDGE,"E91"),sQuery(id+"F0.wireOp",EDGE,"E92"),sQuery(id+"F0.wireOp",EDGE,"E93"),sQuery(id+"F0.wireOp",EDGE,"E94"),sQuery(id+"F0.wireOp",EDGE,"E95"),sQuery(id+"F0.wireOp",EDGE,"E96"),sQuery(id+"F0.wireOp",EDGE,"E97"),sQuery(id+"F0.wireOp",EDGE,"E98"),sQuery(id+"F0.wireOp",EDGE,"E99"),sQuery(id+"F0.wireOp",EDGE,"E100"),sQuery(id+"F0.wireOp",EDGE,"E101"),sQuery(id+"F0.wireOp",EDGE,"E102"),sQuery(id+"F0.wireOp",EDGE,"E103"),sQuery(id+"F0.wireOp",EDGE,"E104"),sQuery(id+"F0.wireOp",EDGE,"E105"),sQuery(id+"F0.wireOp",EDGE,"E106"),sQuery(id+"F0.wireOp",EDGE,"E107"),sQuery(id+"F0.wireOp",EDGE,"E108"),sQuery(id+"F0.wireOp",EDGE,"E109"),sQuery(id+"F0.wireOp",EDGE,"E116"),sQuery(id+"F0.wireOp",EDGE,"E117"),sQuery(id+"F0.wireOp",EDGE,"E119"),sQuery(id+"F0.wireOp",EDGE,"E120"),sQuery(id+"F0.wireOp",EDGE,"E122"),sQuery(id+"F0.wireOp",EDGE,"E123"),sQuery(id+"F0.wireOp",EDGE,"E124"),sQuery(id+"F0.wireOp",EDGE,"E125"),sQuery(id+"F0.wireOp",EDGE,"E126"),sQuery(id+"F0.wireOp",EDGE,"E127"),sQuery(id+"F0.wireOp",EDGE,"E128"),sQuery(id+"F0.wireOp",EDGE,"E129"),sQuery(id+"F0.wireOp",EDGE,"E130"),sQuery(id+"F0.wireOp",EDGE,"E131"),sQuery(id+"F0.wireOp",EDGE,"E132"),sQuery(id+"F0.wireOp",EDGE,"E133"),sQuery(id+"F0.wireOp",EDGE,"E134"),sQuery(id+"F0.wireOp",EDGE,"E135"),sQuery(id+"F0.wireOp",EDGE,"E136"),sQuery(id+"F0.wireOp",EDGE,"E137"),sQuery(id+"F0.wireOp",EDGE,"E138"),sQuery(id+"F0.wireOp",EDGE,"E139"),sQuery(id+"F0.wireOp",EDGE,"E140"),sQuery(id+"F0.wireOp",EDGE,"E141"),sQuery(id+"F0.wireOp",EDGE,"E142"),sQuery(id+"F0.wireOp",EDGE,"E143"),sQuery(id+"F0.wireOp",EDGE,"E144"),sQuery(id+"F0.wireOp",EDGE,"E145"),sQuery(id+"F0.wireOp",EDGE,"E146"),sQuery(id+"F0.wireOp",EDGE,"E147"),sQuery(id+"F0.wireOp",EDGE,"E148"),sQuery(id+"F0.wireOp",EDGE,"E149"),sQuery(id+"F0.wireOp",EDGE,"E150"),sQuery(id+"F0.wireOp",EDGE,"E151"),sQuery(id+"F0.wireOp",EDGE,"E152"),sQuery(id+"F0.wireOp",EDGE,"E153"),sQuery(id+"F0.wireOp",EDGE,"E154"),sQuery(id+"F0.wireOp",EDGE,"E155"),sQuery(id+"F0.wireOp",EDGE,"E156"),sQuery(id+"F0.wireOp",EDGE,"E157"),sQuery(id+"F0.wireOp",EDGE,"E158"),sQuery(id+"F0.wireOp",EDGE,"E159"),sQuery(id+"F0.wireOp",EDGE,"E160"),sQuery(id+"F0.wireOp",EDGE,"E161"),sQuery(id+"F0.wireOp",EDGE,"E162"),sQuery(id+"F0.wireOp",EDGE,"E163"),sQuery(id+"F0.wireOp",EDGE,"E164"),sQuery(id+"F0.wireOp",EDGE,"E165"),sQuery(id+"F0.wireOp",EDGE,"E166"),sQuery(id+"F0.wireOp",EDGE,"E167"),sQuery(id+"F0.wireOp",EDGE,"E168"),sQuery(id+"F0.wireOp",EDGE,"E169"),sQuery(id+"F0.wireOp",EDGE,"E170"),sQuery(id+"F0.wireOp",EDGE,"E171"),sQuery(id+"F0.wireOp",EDGE,"E172"),sQuery(id+"F0.wireOp",EDGE,"E173"),sQuery(id+"F0.wireOp",EDGE,"E174"),sQuery(id+"F0.wireOp",EDGE,"E175"),sQuery(id+"F0.wireOp",EDGE,"E176"),sQuery(id+"F0.wireOp",EDGE,"E177"),sQuery(id+"F0.wireOp",EDGE,"E178"),sQuery(id+"F0.wireOp",EDGE,"E179"),sQuery(id+"F0.wireOp",EDGE,"E180"),sQuery(id+"F0.wireOp",EDGE,"E181"),sQuery(id+"F0.wireOp",EDGE,"E182"),sQuery(id+"F0.wireOp",EDGE,"E183"),sQuery(id+"F0.wireOp",EDGE,"E184"),sQuery(id+"F0.wireOp",EDGE,"E185"),sQuery(id+"F0.wireOp",EDGE,"E186"),sQuery(id+"F0.wireOp",EDGE,"E187"),sQuery(id+"F0.wireOp",EDGE,"E188"),sQuery(id+"F0.wireOp",EDGE,"E189"),sQuery(id+"F0.wireOp",EDGE,"E190"),sQuery(id+"F0.wireOp",EDGE,"E191"),sQuery(id+"F0.wireOp",EDGE,"E192"),sQuery(id+"F0.wireOp",EDGE,"E193"),sQuery(id+"F0.wireOp",EDGE,"E194"),sQuery(id+"F0.wireOp",EDGE,"E195"),sQuery(id+"F0.wireOp",EDGE,"E196"),sQuery(id+"F0.wireOp",EDGE,"E197"),sQuery(id+"F0.wireOp",EDGE,"E198"),sQuery(id+"F0.wireOp",EDGE,"E199"),sQuery(id+"F0.wireOp",EDGE,"E200"),sQuery(id+"F0.wireOp",EDGE,"E201"),sQuery(id+"F0.wireOp",EDGE,"E202"),sQuery(id+"F0.wireOp",EDGE,"E203"),sQuery(id+"F0.wireOp",EDGE,"E204"),sQuery(id+"F0.wireOp",EDGE,"E205"),sQuery(id+"F0.wireOp",EDGE,"E206"),sQuery(id+"F0.wireOp",EDGE,"E207"),sQuery(id+"F0.wireOp",EDGE,"E208"),sQuery(id+"F0.wireOp",EDGE,"E209"),sQuery(id+"F0.wireOp",EDGE,"E210"),sQuery(id+"F0.wireOp",EDGE,"E211"),sQuery(id+"F0.wireOp",EDGE,"E212"),sQuery(id+"F0.wireOp",EDGE,"E213"),sQuery(id+"F0.wireOp",EDGE,"E214"),sQuery(id+"F0.wireOp",EDGE,"E215"),sQuery(id+"F0.wireOp",EDGE,"E216"),sQuery(id+"F0.wireOp",EDGE,"E217"),sQuery(id+"F0.wireOp",EDGE,"E218"),sQuery(id+"F0.wireOp",EDGE,"E219"),sQuery(id+"F0.wireOp",EDGE,"E220"),sQuery(id+"F0.wireOp",EDGE,"E221"),sQuery(id+"F0.wireOp",EDGE,"E222"),sQuery(id+"F0.wireOp",EDGE,"E223"),sQuery(id+"F0.wireOp",EDGE,"E224"),sQuery(id+"F0.wireOp",EDGE,"E225"),sQuery(id+"F0.wireOp",EDGE,"E226"),sQuery(id+"F0.wireOp",EDGE,"E227"),sQuery(id+"F0.wireOp",EDGE,"E228"),sQuery(id+"F0.wireOp",EDGE,"E229"),sQuery(id+"F0.wireOp",EDGE,"E230"),sQuery(id+"F0.wireOp",EDGE,"E231"),sQuery(id+"F0.wireOp",EDGE,"E232"),sQuery(id+"F0.wireOp",EDGE,"E233"),sQuery(id+"F0.wireOp",EDGE,"E234"),sQuery(id+"F0.wireOp",EDGE,"E235"),sQuery(id+"F0.wireOp",EDGE,"E236"),sQuery(id+"F0.wireOp",EDGE,"E237"),sQuery(id+"F0.wireOp",EDGE,"E238"),sQuery(id+"F0.wireOp",EDGE,"E239"),sQuery(id+"F0.wireOp",EDGE,"E240"),sQuery(id+"F0.wireOp",EDGE,"E241"),sQuery(id+"F0.wireOp",EDGE,"E242"),sQuery(id+"F0.wireOp",EDGE,"E243"),sQuery(id+"F0.wireOp",EDGE,"E244"),sQuery(id+"F0.wireOp",EDGE,"E245"),sQuery(id+"F0.wireOp",EDGE,"E246"),sQuery(id+"F0.wireOp",EDGE,"E247"),sQuery(id+"F0.wireOp",EDGE,"E248"),sQuery(id+"F0.wireOp",EDGE,"E249"),sQuery(id+"F0.wireOp",EDGE,"E250"),sQuery(id+"F0.wireOp",EDGE,"E251"),sQuery(id+"F0.wireOp",EDGE,"E252"),sQuery(id+"F0.wireOp",EDGE,"E253"),sQuery(id+"F0.wireOp",EDGE,"E254"),sQuery(id+"F0.wireOp",EDGE,"E255"),sQuery(id+"F0.wireOp",EDGE,"E256"),sQuery(id+"F0.wireOp",EDGE,"E257"),sQuery(id+"F0.wireOp",EDGE,"E258"),sQuery(id+"F0.wireOp",EDGE,"E259"),sQuery(id+"F0.wireOp",EDGE,"E260"),sQuery(id+"F0.wireOp",EDGE,"E261"),sQuery(id+"F0.wireOp",EDGE,"E262"),sQuery(id+"F0.wireOp",EDGE,"E263"),sQuery(id+"F0.wireOp",EDGE,"E264"),sQuery(id+"F0.wireOp",EDGE,"E265"),sQuery(id+"F0.wireOp",EDGE,"E266"),sQuery(id+"F0.wireOp",EDGE,"E267"),sQuery(id+"F0.wireOp",EDGE,"E268"),sQuery(id+"F0.wireOp",EDGE,"E269"),sQuery(id+"F0.wireOp",EDGE,"E270"),sQuery(id+"F0.wireOp",EDGE,"E271"),sQuery(id+"F0.wireOp",EDGE,"E272"),sQuery(id+"F0.wireOp",EDGE,"E273"),sQuery(id+"F0.wireOp",EDGE,"E274"),sQuery(id+"F0.wireOp",EDGE,"E275"),sQuery(id+"F0.wireOp",EDGE,"E276"),sQuery(id+"F0.wireOp",EDGE,"E277"),sQuery(id+"F0.wireOp",EDGE,"E278"),sQuery(id+"F0.wireOp",EDGE,"E279"),sQuery(id+"F0.wireOp",EDGE,"E280"),sQuery(id+"F0.wireOp",EDGE,"E281"),sQuery(id+"F0.wireOp",EDGE,"E282"),sQuery(id+"F0.wireOp",EDGE,"E283"),sQuery(id+"F0.wireOp",EDGE,"E284"),sQuery(id+"F0.wireOp",EDGE,"E285"),sQuery(id+"F0.wireOp",EDGE,"E286"),sQuery(id+"F0.wireOp",EDGE,"E287"),sQuery(id+"F0.wireOp",EDGE,"E288"),sQuery(id+"F0.wireOp",EDGE,"E289"),sQuery(id+"F0.wireOp",EDGE,"E290"),sQuery(id+"F0.wireOp",EDGE,"E291"),sQuery(id+"F0.wireOp",EDGE,"E292"),sQuery(id+"F0.wireOp",EDGE,"E293"),sQuery(id+"F0.wireOp",EDGE,"E294"),sQuery(id+"F0.wireOp",EDGE,"E295"),sQuery(id+"F0.wireOp",EDGE,"E296"),sQuery(id+"F0.wireOp",EDGE,"E297"),sQuery(id+"F0.wireOp",EDGE,"E298"),sQuery(id+"F0.wireOp",EDGE,"E299"),sQuery(id+"F0.wireOp",EDGE,"E300"),sQuery(id+"F0.wireOp",EDGE,"E301"),sQuery(id+"F0.wireOp",EDGE,"E302"),sQuery(id+"F0.wireOp",EDGE,"E303"),sQuery(id+"F0.wireOp",EDGE,"E304"),sQuery(id+"F0.wireOp",EDGE,"E305"),sQuery(id+"F0.wireOp",EDGE,"E306"),sQuery(id+"F0.wireOp",EDGE,"E307"),sQuery(id+"F0.wireOp",EDGE,"E308"),sQuery(id+"F0.wireOp",EDGE,"E309"),sQuery(id+"F0.wireOp",EDGE,"E310"),sQuery(id+"F0.wireOp",EDGE,"E311"),sQuery(id+"F0.wireOp",EDGE,"E312"),sQuery(id+"F0.wireOp",EDGE,"E313"),sQuery(id+"F0.wireOp",EDGE,"E314"),sQuery(id+"F0.wireOp",EDGE,"E315"),sQuery(id+"F0.wireOp",EDGE,"E316"),sQuery(id+"F0.wireOp",EDGE,"E317"),sQuery(id+"F0.wireOp",EDGE,"E318"),sQuery(id+"F0.wireOp",EDGE,"E319"),sQuery(id+"F0.wireOp",EDGE,"E320"),sQuery(id+"F0.wireOp",EDGE,"E321"),sQuery(id+"F0.wireOp",EDGE,"E322"),sQuery(id+"F0.wireOp",EDGE,"E323"),sQuery(id+"F0.wireOp",EDGE,"E324"),sQuery(id+"F0.wireOp",EDGE,"E325"),sQuery(id+"F0.wireOp",EDGE,"E326"),sQuery(id+"F0.wireOp",EDGE,"E327"),sQuery(id+"F0.wireOp",EDGE,"E328"),sQuery(id+"F0.wireOp",EDGE,"E329"),sQuery(id+"F0.wireOp",EDGE,"E330"),sQuery(id+"F0.wireOp",EDGE,"E331"),sQuery(id+"F0.wireOp",EDGE,"E332"),sQuery(id+"F0.wireOp",EDGE,"E333"),sQuery(id+"F0.wireOp",EDGE,"E334"),sQuery(id+"F0.wireOp",EDGE,"E335"),sQuery(id+"F0.wireOp",EDGE,"E336"),sQuery(id+"F0.wireOp",EDGE,"E337"),sQuery(id+"F0.wireOp",EDGE,"E338"),sQuery(id+"F0.wireOp",EDGE,"E339"),sQuery(id+"F0.wireOp",EDGE,"E340"),sQuery(id+"F0.wireOp",EDGE,"E341"),sQuery(id+"F0.wireOp",EDGE,"E342"),sQuery(id+"F0.wireOp",EDGE,"E343"),sQuery(id+"F0.wireOp",EDGE,"E344"),sQuery(id+"F0.wireOp",EDGE,"E345"),sQuery(id+"F0.wireOp",EDGE,"E346"),sQuery(id+"F0.wireOp",EDGE,"E347"),sQuery(id+"F0.wireOp",EDGE,"E348"),sQuery(id+"F0.wireOp",EDGE,"E349"),sQuery(id+"F0.wireOp",EDGE,"E350"),sQuery(id+"F0.wireOp",EDGE,"E351"),sQuery(id+"F0.wireOp",EDGE,"E352"),sQuery(id+"F0.wireOp",EDGE,"E353"),sQuery(id+"F0.wireOp",EDGE,"E354"),sQuery(id+"F0.wireOp",EDGE,"E355"),sQuery(id+"F0.wireOp",EDGE,"E356"),sQuery(id+"F0.wireOp",EDGE,"E359"),sQuery(id+"F0.wireOp",EDGE,"E360"),sQuery(id+"F0.wireOp",EDGE,"E361"),sQuery(id+"F0.wireOp",EDGE,"E362"),sQuery(id+"F0.wireOp",EDGE,"E363"),sQuery(id+"F0.wireOp",EDGE,"E364"),sQuery(id+"F0.wireOp",EDGE,"E368"),sQuery(id+"F0.wireOp",EDGE,"E370"),sQuery(id+"F0.wireOp",EDGE,"E374"),sQuery(id+"F0.wireOp",EDGE,"E408"),sQuery(id+"F0.wireOp",EDGE,"E409"),sQuery(id+"F0.wireOp",EDGE,"E410"),sQuery(id+"F0.wireOp",EDGE,"E411"),sQuery(id+"F0.wireOp",EDGE,"E412"),sQuery(id+"F0.wireOp",EDGE,"E413"),sQuery(id+"F0.wireOp",EDGE,"E414"),sQuery(id+"F0.wireOp",EDGE,"E415"),sQuery(id+"F0.wireOp",EDGE,"E416"),sQuery(id+"F0.wireOp",EDGE,"E417"),sQuery(id+"F0.wireOp",EDGE,"E418"),sQuery(id+"F0.wireOp",EDGE,"E419"),sQuery(id+"F0.wireOp",EDGE,"E420"),sQuery(id+"F0.wireOp",EDGE,"E421"),sQuery(id+"F0.wireOp",EDGE,"E422"),sQuery(id+"F0.wireOp",EDGE,"E423"),sQuery(id+"F0.wireOp",EDGE,"E424"),sQuery(id+"F0.wireOp",EDGE,"E425"),sQuery(id+"F0.wireOp",EDGE,"E426"),sQuery(id+"F0.wireOp",EDGE,"E427"),sQuery(id+"F0.wireOp",EDGE,"E428"),sQuery(id+"F0.wireOp",EDGE,"E429"),sQuery(id+"F0.wireOp",EDGE,"E430"),sQuery(id+"F0.wireOp",EDGE,"E431"),sQuery(id+"F0.wireOp",EDGE,"E432"),sQuery(id+"F0.wireOp",EDGE,"E433"),sQuery(id+"F0.wireOp",EDGE,"E434"),sQuery(id+"F0.wireOp",EDGE,"E435"),sQuery(id+"F0.wireOp",EDGE,"E436"),sQuery(id+"F0.wireOp",EDGE,"E437"),sQuery(id+"F0.wireOp",EDGE,"E438"),sQuery(id+"F0.wireOp",EDGE,"E439"),sQuery(id+"F0.wireOp",EDGE,"E440"),sQuery(id+"F0.wireOp",EDGE,"E441"),sQuery(id+"F0.wireOp",EDGE,"E442"),sQuery(id+"F0.wireOp",EDGE,"E443"),sQuery(id+"F0.wireOp",EDGE,"E444"),sQuery(id+"F0.wireOp",EDGE,"E445"),sQuery(id+"F0.wireOp",EDGE,"E446"),sQuery(id+"F0.wireOp",EDGE,"E447"),sQuery(id+"F0.wireOp",EDGE,"E448"),sQuery(id+"F0.wireOp",EDGE,"E449"),sQuery(id+"F0.wireOp",EDGE,"E450"),sQuery(id+"F0.wireOp",EDGE,"E451"),sQuery(id+"F0.wireOp",EDGE,"E452"),sQuery(id+"F0.wireOp",EDGE,"E453"),sQuery(id+"F0.wireOp",EDGE,"E454"),sQuery(id+"F0.wireOp",EDGE,"E455"),sQuery(id+"F0.wireOp",EDGE,"E456"),sQuery(id+"F0.wireOp",EDGE,"E457"),sQuery(id+"F0.wireOp",EDGE,"E458"),sQuery(id+"F0.wireOp",EDGE,"E459"),sQuery(id+"F0.wireOp",EDGE,"E460"),sQuery(id+"F0.wireOp",EDGE,"E461"),sQuery(id+"F0.wireOp",EDGE,"E462"),sQuery(id+"F0.wireOp",EDGE,"E463"),sQuery(id+"F0.wireOp",EDGE,"E464"),sQuery(id+"F0.wireOp",EDGE,"E465"),sQuery(id+"F0.wireOp",EDGE,"E466"),sQuery(id+"F0.wireOp",EDGE,"E467"),sQuery(id+"F0.wireOp",EDGE,"E468"),sQuery(id+"F0.wireOp",EDGE,"E469"),sQuery(id+"F0.wireOp",EDGE,"E470"),sQuery(id+"F0.wireOp",EDGE,"E471"),sQuery(id+"F0.wireOp",EDGE,"E472"),sQuery(id+"F0.wireOp",EDGE,"E473"),sQuery(id+"F0.wireOp",EDGE,"E474"),sQuery(id+"F0.wireOp",EDGE,"E475"),sQuery(id+"F0.wireOp",EDGE,"E476"),sQuery(id+"F0.wireOp",EDGE,"E477"),sQuery(id+"F0.wireOp",EDGE,"E478"),sQuery(id+"F0.wireOp",EDGE,"E479"),sQuery(id+"F0.wireOp",EDGE,"E480"),sQuery(id+"F0.wireOp",EDGE,"E481"),sQuery(id+"F0.wireOp",EDGE,"E482"),sQuery(id+"F0.wireOp",EDGE,"E483"),sQuery(id+"F0.wireOp",EDGE,"E484"),sQuery(id+"F0.wireOp",EDGE,"E485"),sQuery(id+"F0.wireOp",EDGE,"E486"),sQuery(id+"F0.wireOp",EDGE,"E487"),sQuery(id+"F0.wireOp",EDGE,"E488"),sQuery(id+"F0.wireOp",EDGE,"E489"),sQuery(id+"F0.wireOp",EDGE,"E490"),sQuery(id+"F0.wireOp",EDGE,"E491"),sQuery(id+"F0.wireOp",EDGE,"E492"),sQuery(id+"F0.wireOp",EDGE,"E493"),sQuery(id+"F0.wireOp",EDGE,"E494"),sQuery(id+"F0.wireOp",EDGE,"E495"),sQuery(id+"F0.wireOp",EDGE,"E496"),sQuery(id+"F0.wireOp",EDGE,"E497"),sQuery(id+"F0.wireOp",EDGE,"E498"),sQuery(id+"F0.wireOp",EDGE,"E499"),sQuery(id+"F0.wireOp",EDGE,"E500"),sQuery(id+"F0.wireOp",EDGE,"E501"),sQuery(id+"F0.wireOp",EDGE,"E502"),sQuery(id+"F0.wireOp",EDGE,"E503"),sQuery(id+"F0.wireOp",EDGE,"E504"),sQuery(id+"F0.wireOp",EDGE,"E505"),sQuery(id+"F0.wireOp",EDGE,"E506"),sQuery(id+"F0.wireOp",EDGE,"E507"),sQuery(id+"F0.wireOp",EDGE,"E508"),sQuery(id+"F0.wireOp",EDGE,"E509"),sQuery(id+"F0.wireOp",EDGE,"E510"),sQuery(id+"F0.wireOp",EDGE,"E511"),sQuery(id+"F0.wireOp",EDGE,"E512"),sQuery(id+"F0.wireOp",EDGE,"E513"),sQuery(id+"F0.wireOp",EDGE,"E514"),sQuery(id+"F0.wireOp",EDGE,"E515"),sQuery(id+"F0.wireOp",EDGE,"E516"),sQuery(id+"F0.wireOp",EDGE,"E517"),sQuery(id+"F0.wireOp",EDGE,"E518"),sQuery(id+"F0.wireOp",EDGE,"E519"),sQuery(id+"F0.wireOp",EDGE,"E520"),sQuery(id+"F0.wireOp",EDGE,"E521"),sQuery(id+"F0.wireOp",EDGE,"E522"),sQuery(id+"F0.wireOp",EDGE,"E523"),sQuery(id+"F0.wireOp",EDGE,"E524"),sQuery(id+"F0.wireOp",EDGE,"E525"),sQuery(id+"F0.wireOp",EDGE,"E526"),sQuery(id+"F0.wireOp",EDGE,"E527"),sQuery(id+"F0.wireOp",EDGE,"E528"),sQuery(id+"F0.wireOp",EDGE,"E529"),sQuery(id+"F0.wireOp",EDGE,"E530"),sQuery(id+"F0.wireOp",EDGE,"E531"),sQuery(id+"F0.wireOp",EDGE,"E532"),sQuery(id+"F0.wireOp",EDGE,"E533"),sQuery(id+"F0.wireOp",EDGE,"E534"),sQuery(id+"F0.wireOp",EDGE,"E535"),sQuery(id+"F0.wireOp",EDGE,"E536"),sQuery(id+"F0.wireOp",EDGE,"E537"),sQuery(id+"F0.wireOp",EDGE,"E538"),sQuery(id+"F0.wireOp",EDGE,"E539"),sQuery(id+"F0.wireOp",EDGE,"E540"),sQuery(id+"F0.wireOp",EDGE,"E541"),sQuery(id+"F0.wireOp",EDGE,"E542"),sQuery(id+"F0.wireOp",EDGE,"E543"),sQuery(id+"F0.wireOp",EDGE,"E544"),sQuery(id+"F0.wireOp",EDGE,"E545"),sQuery(id+"F0.wireOp",EDGE,"E546"),sQuery(id+"F0.wireOp",EDGE,"E547"),sQuery(id+"F0.wireOp",EDGE,"E548"),sQuery(id+"F0.wireOp",EDGE,"E549"),sQuery(id+"F0.wireOp",EDGE,"E550"),sQuery(id+"F0.wireOp",EDGE,"E551"),sQuery(id+"F0.wireOp",EDGE,"E552"),sQuery(id+"F0.wireOp",EDGE,"E553"),sQuery(id+"F0.wireOp",EDGE,"E554"),sQuery(id+"F0.wireOp",EDGE,"E555"),sQuery(id+"F0.wireOp",EDGE,"E556"),sQuery(id+"F0.wireOp",EDGE,"E557"),sQuery(id+"F0.wireOp",EDGE,"E558"),sQuery(id+"F0.wireOp",EDGE,"E559"),sQuery(id+"F0.wireOp",EDGE,"E560"),sQuery(id+"F0.wireOp",EDGE,"E561"),sQuery(id+"F0.wireOp",EDGE,"E562"),sQuery(id+"F0.wireOp",EDGE,"E563"),sQuery(id+"F0.wireOp",EDGE,"E564"),sQuery(id+"F0.wireOp",EDGE,"E565"),sQuery(id+"F0.wireOp",EDGE,"E566"),sQuery(id+"F0.wireOp",EDGE,"E567"),sQuery(id+"F0.wireOp",EDGE,"E568"),sQuery(id+"F0.wireOp",EDGE,"E569"),sQuery(id+"F0.wireOp",EDGE,"E570"),sQuery(id+"F0.wireOp",EDGE,"E571"),sQuery(id+"F0.wireOp",EDGE,"E572"),sQuery(id+"F0.wireOp",EDGE,"E573"),sQuery(id+"F0.wireOp",EDGE,"E574"),sQuery(id+"F0.wireOp",EDGE,"E575"),sQuery(id+"F0.wireOp",EDGE,"E576"),sQuery(id+"F0.wireOp",EDGE,"E577"),sQuery(id+"F0.wireOp",EDGE,"E578"),sQuery(id+"F0.wireOp",EDGE,"E579"),sQuery(id+"F0.wireOp",EDGE,"E580"),sQuery(id+"F0.wireOp",EDGE,"E581"),sQuery(id+"F0.wireOp",EDGE,"E582"),sQuery(id+"F0.wireOp",EDGE,"E583"),sQuery(id+"F0.wireOp",EDGE,"E584"),sQuery(id+"F0.wireOp",EDGE,"E585"),sQuery(id+"F0.wireOp",EDGE,"E586"),sQuery(id+"F0.wireOp",EDGE,"E587"),sQuery(id+"F0.wireOp",EDGE,"E588"),sQuery(id+"F0.wireOp",EDGE,"E589"),sQuery(id+"F0.wireOp",EDGE,"E590"),sQuery(id+"F0.wireOp",EDGE,"E591"),sQuery(id+"F0.wireOp",EDGE,"E592"),sQuery(id+"F0.wireOp",EDGE,"E597"),sQuery(id+"F0.wireOp",EDGE,"E599"),sQuery(id+"F0.wireOp",EDGE,"E600"),sQuery(id+"F0.wireOp",EDGE,"E601"),sQuery(id+"F0.wireOp",EDGE,"E604"),sQuery(id+"F0.wireOp",EDGE,"E605"),sQuery(id+"F0.wireOp",EDGE,"E606"),sQuery(id+"F0.wireOp",EDGE,"E607"),sQuery(id+"F0.wireOp",EDGE,"E608"),sQuery(id+"F0.wireOp",EDGE,"E609"),sQuery(id+"F0.wireOp",EDGE,"E612"),sQuery(id+"F0.wireOp",EDGE,"E614"),sQuery(id+"F0.wireOp",EDGE,"E615"),sQuery(id+"F0.wireOp",EDGE,"E616"),sQuery(id+"F0.wireOp",EDGE,"E617"),sQuery(id+"F0.wireOp",EDGE,"E618"),sQuery(id+"F0.wireOp",EDGE,"E619"),sQuery(id+"F0.wireOp",EDGE,"E620"),sQuery(id+"F0.wireOp",EDGE,"E621"),sQuery(id+"F0.wireOp",EDGE,"E622"),sQuery(id+"F0.wireOp",EDGE,"E623"),sQuery(id+"F0.wireOp",EDGE,"E624"),sQuery(id+"F0.wireOp",EDGE,"E625"),sQuery(id+"F0.wireOp",EDGE,"E626"),sQuery(id+"F0.wireOp",EDGE,"E627"),sQuery(id+"F0.wireOp",EDGE,"E628"),sQuery(id+"F0.wireOp",EDGE,"E629"),sQuery(id+"F0.wireOp",EDGE,"E630"),sQuery(id+"F0.wireOp",EDGE,"E635"),sQuery(id+"F0.wireOp",EDGE,"E636"),sQuery(id+"F0.wireOp",EDGE,"E638"),sQuery(id+"F0.wireOp",EDGE,"E639"),sQuery(id+"F0.wireOp",EDGE,"E640"),sQuery(id+"F0.wireOp",EDGE,"E641"),sQuery(id+"F0.wireOp",EDGE,"E642"),sQuery(id+"F0.wireOp",EDGE,"E643"),sQuery(id+"F0.wireOp",EDGE,"E644"),sQuery(id+"F0.wireOp",EDGE,"E645"),sQuery(id+"F0.wireOp",EDGE,"E646"),sQuery(id+"F0.wireOp",EDGE,"E653"),sQuery(id+"F0.wireOp",EDGE,"E654"),sQuery(id+"F0.wireOp",EDGE,"E655"),sQuery(id+"F0.wireOp",EDGE,"E656"),sQuery(id+"F0.wireOp",EDGE,"E657"),sQuery(id+"F0.wireOp",EDGE,"E658"),sQuery(id+"F0.wireOp",EDGE,"E659"),sQuery(id+"F0.wireOp",EDGE,"E660"),sQuery(id+"F0.wireOp",EDGE,"E661"),sQuery(id+"F0.wireOp",EDGE,"E662"),sQuery(id+"F0.wireOp",EDGE,"E663"),sQuery(id+"F0.wireOp",EDGE,"E664"),sQuery(id+"F0.wireOp",EDGE,"E665"),sQuery(id+"F0.wireOp",EDGE,"E666"),sQuery(id+"F0.wireOp",EDGE,"E667"),sQuery(id+"F0.wireOp",EDGE,"E668"),sQuery(id+"F0.wireOp",EDGE,"E669"),sQuery(id+"F0.wireOp",EDGE,"E670"),sQuery(id+"F0.wireOp",EDGE,"E671"),sQuery(id+"F0.wireOp",EDGE,"E672"),sQuery(id+"F0.wireOp",EDGE,"E673"),sQuery(id+"F0.wireOp",EDGE,"E674")])],"isStart":false});
            var sketch = newSketch(context, id + "F2", { "sketchPlane" : qUnion([Q0])});
            skLineSegment(sketch, "E677", {"start": v(-7.33, 0) * mm, "end": v(35.33, 0) * mm, "construction": true});
            skPoint(sketch, "E678", {"position": v(14, 0) * mm});
            skCircle(sketch, "E679", {"center": v(14, 0) * mm, "radius": 17.5 * mm});
            skSolve(sketch);
        }
        {
            var Q0;
            Q0=makeQuery(id+"F2.imprint","IMPRINT",FACE,{"disambiguationData":[TD([[makeQuery(id+"F2.imprint","IMPRINT",EDGE,{"derivedFrom":sQuery(id+"F2.wireOp",EDGE,"E679")}),1.0]])]});
            var Q1;
            Q1=qConstructionFilter(qBodyType(qCreatedBy(id+"F2",EDGE),BodyType.WIRE),ConstructionObject.NO);
            extrude(context, id + "F3", {"entities" : qUnion([Q0]), "operationType" : NewBodyOperationType.ADD, "surfaceEntities" : qUnion([Q1]), "depth" : 3.5 * mm, "offsetDistance" : 25 * mm});
        }
        {
            var Q0;
            Q0=makeQuery(id+"F1.opExtrude","CAP_FACE",FACE,{"disambiguationData":[OSD([sQuery(id+"F0.wireOp",EDGE,"E2"),sQuery(id+"F0.wireOp",EDGE,"E8"),sQuery(id+"F0.wireOp",EDGE,"E10"),sQuery(id+"F0.wireOp",EDGE,"E21"),sQuery(id+"F0.wireOp",EDGE,"E22"),sQuery(id+"F0.wireOp",EDGE,"E27"),sQuery(id+"F0.wireOp",EDGE,"E28"),sQuery(id+"F0.wireOp",EDGE,"E29"),sQuery(id+"F0.wireOp",EDGE,"E30"),sQuery(id+"F0.wireOp",EDGE,"E31"),sQuery(id+"F0.wireOp",EDGE,"E32"),sQuery(id+"F0.wireOp",EDGE,"E33"),sQuery(id+"F0.wireOp",EDGE,"E34"),sQuery(id+"F0.wireOp",EDGE,"E35"),sQuery(id+"F0.wireOp",EDGE,"E36"),sQuery(id+"F0.wireOp",EDGE,"E37"),sQuery(id+"F0.wireOp",EDGE,"E38"),sQuery(id+"F0.wireOp",EDGE,"E39"),sQuery(id+"F0.wireOp",EDGE,"E40"),sQuery(id+"F0.wireOp",EDGE,"E41"),sQuery(id+"F0.wireOp",EDGE,"E42"),sQuery(id+"F0.wireOp",EDGE,"E43"),sQuery(id+"F0.wireOp",EDGE,"E44"),sQuery(id+"F0.wireOp",EDGE,"E45"),sQuery(id+"F0.wireOp",EDGE,"E46"),sQuery(id+"F0.wireOp",EDGE,"E47"),sQuery(id+"F0.wireOp",EDGE,"E48"),sQuery(id+"F0.wireOp",EDGE,"E49"),sQuery(id+"F0.wireOp",EDGE,"E50"),sQuery(id+"F0.wireOp",EDGE,"E51"),sQuery(id+"F0.wireOp",EDGE,"E52"),sQuery(id+"F0.wireOp",EDGE,"E53"),sQuery(id+"F0.wireOp",EDGE,"E54"),sQuery(id+"F0.wireOp",EDGE,"E55"),sQuery(id+"F0.wireOp",EDGE,"E56"),sQuery(id+"F0.wireOp",EDGE,"E57"),sQuery(id+"F0.wireOp",EDGE,"E58"),sQuery(id+"F0.wireOp",EDGE,"E59"),sQuery(id+"F0.wireOp",EDGE,"E60"),sQuery(id+"F0.wireOp",EDGE,"E61"),sQuery(id+"F0.wireOp",EDGE,"E62"),sQuery(id+"F0.wireOp",EDGE,"E63"),sQuery(id+"F0.wireOp",EDGE,"E64"),sQuery(id+"F0.wireOp",EDGE,"E65"),sQuery(id+"F0.wireOp",EDGE,"E66"),sQuery(id+"F0.wireOp",EDGE,"E83"),sQuery(id+"F0.wireOp",EDGE,"E84"),sQuery(id+"F0.wireOp",EDGE,"E85"),sQuery(id+"F0.wireOp",EDGE,"E86"),sQuery(id+"F0.wireOp",EDGE,"E87"),sQuery(id+"F0.wireOp",EDGE,"E88"),sQuery(id+"F0.wireOp",EDGE,"E89"),sQuery(id+"F0.wireOp",EDGE,"E90"),sQuery(id+"F0.wireOp",EDGE,"E91"),sQuery(id+"F0.wireOp",EDGE,"E92"),sQuery(id+"F0.wireOp",EDGE,"E93"),sQuery(id+"F0.wireOp",EDGE,"E94"),sQuery(id+"F0.wireOp",EDGE,"E95"),sQuery(id+"F0.wireOp",EDGE,"E96"),sQuery(id+"F0.wireOp",EDGE,"E97"),sQuery(id+"F0.wireOp",EDGE,"E98"),sQuery(id+"F0.wireOp",EDGE,"E99"),sQuery(id+"F0.wireOp",EDGE,"E100"),sQuery(id+"F0.wireOp",EDGE,"E101"),sQuery(id+"F0.wireOp",EDGE,"E102"),sQuery(id+"F0.wireOp",EDGE,"E103"),sQuery(id+"F0.wireOp",EDGE,"E104"),sQuery(id+"F0.wireOp",EDGE,"E105"),sQuery(id+"F0.wireOp",EDGE,"E106"),sQuery(id+"F0.wireOp",EDGE,"E107"),sQuery(id+"F0.wireOp",EDGE,"E108"),sQuery(id+"F0.wireOp",EDGE,"E109"),sQuery(id+"F0.wireOp",EDGE,"E116"),sQuery(id+"F0.wireOp",EDGE,"E117"),sQuery(id+"F0.wireOp",EDGE,"E119"),sQuery(id+"F0.wireOp",EDGE,"E120"),sQuery(id+"F0.wireOp",EDGE,"E122"),sQuery(id+"F0.wireOp",EDGE,"E123"),sQuery(id+"F0.wireOp",EDGE,"E124"),sQuery(id+"F0.wireOp",EDGE,"E125"),sQuery(id+"F0.wireOp",EDGE,"E126"),sQuery(id+"F0.wireOp",EDGE,"E127"),sQuery(id+"F0.wireOp",EDGE,"E128"),sQuery(id+"F0.wireOp",EDGE,"E129"),sQuery(id+"F0.wireOp",EDGE,"E130"),sQuery(id+"F0.wireOp",EDGE,"E131"),sQuery(id+"F0.wireOp",EDGE,"E132"),sQuery(id+"F0.wireOp",EDGE,"E133"),sQuery(id+"F0.wireOp",EDGE,"E134"),sQuery(id+"F0.wireOp",EDGE,"E135"),sQuery(id+"F0.wireOp",EDGE,"E136"),sQuery(id+"F0.wireOp",EDGE,"E137"),sQuery(id+"F0.wireOp",EDGE,"E138"),sQuery(id+"F0.wireOp",EDGE,"E139"),sQuery(id+"F0.wireOp",EDGE,"E140"),sQuery(id+"F0.wireOp",EDGE,"E141"),sQuery(id+"F0.wireOp",EDGE,"E142"),sQuery(id+"F0.wireOp",EDGE,"E143"),sQuery(id+"F0.wireOp",EDGE,"E144"),sQuery(id+"F0.wireOp",EDGE,"E145"),sQuery(id+"F0.wireOp",EDGE,"E146"),sQuery(id+"F0.wireOp",EDGE,"E147"),sQuery(id+"F0.wireOp",EDGE,"E148"),sQuery(id+"F0.wireOp",EDGE,"E149"),sQuery(id+"F0.wireOp",EDGE,"E150"),sQuery(id+"F0.wireOp",EDGE,"E151"),sQuery(id+"F0.wireOp",EDGE,"E152"),sQuery(id+"F0.wireOp",EDGE,"E153"),sQuery(id+"F0.wireOp",EDGE,"E154"),sQuery(id+"F0.wireOp",EDGE,"E155"),sQuery(id+"F0.wireOp",EDGE,"E156"),sQuery(id+"F0.wireOp",EDGE,"E157"),sQuery(id+"F0.wireOp",EDGE,"E158"),sQuery(id+"F0.wireOp",EDGE,"E159"),sQuery(id+"F0.wireOp",EDGE,"E160"),sQuery(id+"F0.wireOp",EDGE,"E161"),sQuery(id+"F0.wireOp",EDGE,"E162"),sQuery(id+"F0.wireOp",EDGE,"E163"),sQuery(id+"F0.wireOp",EDGE,"E164"),sQuery(id+"F0.wireOp",EDGE,"E165"),sQuery(id+"F0.wireOp",EDGE,"E166"),sQuery(id+"F0.wireOp",EDGE,"E167"),sQuery(id+"F0.wireOp",EDGE,"E168"),sQuery(id+"F0.wireOp",EDGE,"E169"),sQuery(id+"F0.wireOp",EDGE,"E170"),sQuery(id+"F0.wireOp",EDGE,"E171"),sQuery(id+"F0.wireOp",EDGE,"E172"),sQuery(id+"F0.wireOp",EDGE,"E173"),sQuery(id+"F0.wireOp",EDGE,"E174"),sQuery(id+"F0.wireOp",EDGE,"E175"),sQuery(id+"F0.wireOp",EDGE,"E176"),sQuery(id+"F0.wireOp",EDGE,"E177"),sQuery(id+"F0.wireOp",EDGE,"E178"),sQuery(id+"F0.wireOp",EDGE,"E179"),sQuery(id+"F0.wireOp",EDGE,"E180"),sQuery(id+"F0.wireOp",EDGE,"E181"),sQuery(id+"F0.wireOp",EDGE,"E182"),sQuery(id+"F0.wireOp",EDGE,"E183"),sQuery(id+"F0.wireOp",EDGE,"E184"),sQuery(id+"F0.wireOp",EDGE,"E185"),sQuery(id+"F0.wireOp",EDGE,"E186"),sQuery(id+"F0.wireOp",EDGE,"E187"),sQuery(id+"F0.wireOp",EDGE,"E188"),sQuery(id+"F0.wireOp",EDGE,"E189"),sQuery(id+"F0.wireOp",EDGE,"E190"),sQuery(id+"F0.wireOp",EDGE,"E191"),sQuery(id+"F0.wireOp",EDGE,"E192"),sQuery(id+"F0.wireOp",EDGE,"E193"),sQuery(id+"F0.wireOp",EDGE,"E194"),sQuery(id+"F0.wireOp",EDGE,"E195"),sQuery(id+"F0.wireOp",EDGE,"E196"),sQuery(id+"F0.wireOp",EDGE,"E197"),sQuery(id+"F0.wireOp",EDGE,"E198"),sQuery(id+"F0.wireOp",EDGE,"E199"),sQuery(id+"F0.wireOp",EDGE,"E200"),sQuery(id+"F0.wireOp",EDGE,"E201"),sQuery(id+"F0.wireOp",EDGE,"E202"),sQuery(id+"F0.wireOp",EDGE,"E203"),sQuery(id+"F0.wireOp",EDGE,"E204"),sQuery(id+"F0.wireOp",EDGE,"E205"),sQuery(id+"F0.wireOp",EDGE,"E206"),sQuery(id+"F0.wireOp",EDGE,"E207"),sQuery(id+"F0.wireOp",EDGE,"E208"),sQuery(id+"F0.wireOp",EDGE,"E209"),sQuery(id+"F0.wireOp",EDGE,"E210"),sQuery(id+"F0.wireOp",EDGE,"E211"),sQuery(id+"F0.wireOp",EDGE,"E212"),sQuery(id+"F0.wireOp",EDGE,"E213"),sQuery(id+"F0.wireOp",EDGE,"E214"),sQuery(id+"F0.wireOp",EDGE,"E215"),sQuery(id+"F0.wireOp",EDGE,"E216"),sQuery(id+"F0.wireOp",EDGE,"E217"),sQuery(id+"F0.wireOp",EDGE,"E218"),sQuery(id+"F0.wireOp",EDGE,"E219"),sQuery(id+"F0.wireOp",EDGE,"E220"),sQuery(id+"F0.wireOp",EDGE,"E221"),sQuery(id+"F0.wireOp",EDGE,"E222"),sQuery(id+"F0.wireOp",EDGE,"E223"),sQuery(id+"F0.wireOp",EDGE,"E224"),sQuery(id+"F0.wireOp",EDGE,"E225"),sQuery(id+"F0.wireOp",EDGE,"E226"),sQuery(id+"F0.wireOp",EDGE,"E227"),sQuery(id+"F0.wireOp",EDGE,"E228"),sQuery(id+"F0.wireOp",EDGE,"E229"),sQuery(id+"F0.wireOp",EDGE,"E230"),sQuery(id+"F0.wireOp",EDGE,"E231"),sQuery(id+"F0.wireOp",EDGE,"E232"),sQuery(id+"F0.wireOp",EDGE,"E233"),sQuery(id+"F0.wireOp",EDGE,"E234"),sQuery(id+"F0.wireOp",EDGE,"E235"),sQuery(id+"F0.wireOp",EDGE,"E236"),sQuery(id+"F0.wireOp",EDGE,"E237"),sQuery(id+"F0.wireOp",EDGE,"E238"),sQuery(id+"F0.wireOp",EDGE,"E239"),sQuery(id+"F0.wireOp",EDGE,"E240"),sQuery(id+"F0.wireOp",EDGE,"E241"),sQuery(id+"F0.wireOp",EDGE,"E242"),sQuery(id+"F0.wireOp",EDGE,"E243"),sQuery(id+"F0.wireOp",EDGE,"E244"),sQuery(id+"F0.wireOp",EDGE,"E245"),sQuery(id+"F0.wireOp",EDGE,"E246"),sQuery(id+"F0.wireOp",EDGE,"E247"),sQuery(id+"F0.wireOp",EDGE,"E248"),sQuery(id+"F0.wireOp",EDGE,"E249"),sQuery(id+"F0.wireOp",EDGE,"E250"),sQuery(id+"F0.wireOp",EDGE,"E251"),sQuery(id+"F0.wireOp",EDGE,"E252"),sQuery(id+"F0.wireOp",EDGE,"E253"),sQuery(id+"F0.wireOp",EDGE,"E254"),sQuery(id+"F0.wireOp",EDGE,"E255"),sQuery(id+"F0.wireOp",EDGE,"E256"),sQuery(id+"F0.wireOp",EDGE,"E257"),sQuery(id+"F0.wireOp",EDGE,"E258"),sQuery(id+"F0.wireOp",EDGE,"E259"),sQuery(id+"F0.wireOp",EDGE,"E260"),sQuery(id+"F0.wireOp",EDGE,"E261"),sQuery(id+"F0.wireOp",EDGE,"E262"),sQuery(id+"F0.wireOp",EDGE,"E263"),sQuery(id+"F0.wireOp",EDGE,"E264"),sQuery(id+"F0.wireOp",EDGE,"E265"),sQuery(id+"F0.wireOp",EDGE,"E266"),sQuery(id+"F0.wireOp",EDGE,"E267"),sQuery(id+"F0.wireOp",EDGE,"E268"),sQuery(id+"F0.wireOp",EDGE,"E269"),sQuery(id+"F0.wireOp",EDGE,"E270"),sQuery(id+"F0.wireOp",EDGE,"E271"),sQuery(id+"F0.wireOp",EDGE,"E272"),sQuery(id+"F0.wireOp",EDGE,"E273"),sQuery(id+"F0.wireOp",EDGE,"E274"),sQuery(id+"F0.wireOp",EDGE,"E275"),sQuery(id+"F0.wireOp",EDGE,"E276"),sQuery(id+"F0.wireOp",EDGE,"E277"),sQuery(id+"F0.wireOp",EDGE,"E278"),sQuery(id+"F0.wireOp",EDGE,"E279"),sQuery(id+"F0.wireOp",EDGE,"E280"),sQuery(id+"F0.wireOp",EDGE,"E281"),sQuery(id+"F0.wireOp",EDGE,"E282"),sQuery(id+"F0.wireOp",EDGE,"E283"),sQuery(id+"F0.wireOp",EDGE,"E284"),sQuery(id+"F0.wireOp",EDGE,"E285"),sQuery(id+"F0.wireOp",EDGE,"E286"),sQuery(id+"F0.wireOp",EDGE,"E287"),sQuery(id+"F0.wireOp",EDGE,"E288"),sQuery(id+"F0.wireOp",EDGE,"E289"),sQuery(id+"F0.wireOp",EDGE,"E290"),sQuery(id+"F0.wireOp",EDGE,"E291"),sQuery(id+"F0.wireOp",EDGE,"E292"),sQuery(id+"F0.wireOp",EDGE,"E293"),sQuery(id+"F0.wireOp",EDGE,"E294"),sQuery(id+"F0.wireOp",EDGE,"E295"),sQuery(id+"F0.wireOp",EDGE,"E296"),sQuery(id+"F0.wireOp",EDGE,"E297"),sQuery(id+"F0.wireOp",EDGE,"E298"),sQuery(id+"F0.wireOp",EDGE,"E299"),sQuery(id+"F0.wireOp",EDGE,"E300"),sQuery(id+"F0.wireOp",EDGE,"E301"),sQuery(id+"F0.wireOp",EDGE,"E302"),sQuery(id+"F0.wireOp",EDGE,"E303"),sQuery(id+"F0.wireOp",EDGE,"E304"),sQuery(id+"F0.wireOp",EDGE,"E305"),sQuery(id+"F0.wireOp",EDGE,"E306"),sQuery(id+"F0.wireOp",EDGE,"E307"),sQuery(id+"F0.wireOp",EDGE,"E308"),sQuery(id+"F0.wireOp",EDGE,"E309"),sQuery(id+"F0.wireOp",EDGE,"E310"),sQuery(id+"F0.wireOp",EDGE,"E311"),sQuery(id+"F0.wireOp",EDGE,"E312"),sQuery(id+"F0.wireOp",EDGE,"E313"),sQuery(id+"F0.wireOp",EDGE,"E314"),sQuery(id+"F0.wireOp",EDGE,"E315"),sQuery(id+"F0.wireOp",EDGE,"E316"),sQuery(id+"F0.wireOp",EDGE,"E317"),sQuery(id+"F0.wireOp",EDGE,"E318"),sQuery(id+"F0.wireOp",EDGE,"E319"),sQuery(id+"F0.wireOp",EDGE,"E320"),sQuery(id+"F0.wireOp",EDGE,"E321"),sQuery(id+"F0.wireOp",EDGE,"E322"),sQuery(id+"F0.wireOp",EDGE,"E323"),sQuery(id+"F0.wireOp",EDGE,"E324"),sQuery(id+"F0.wireOp",EDGE,"E325"),sQuery(id+"F0.wireOp",EDGE,"E326"),sQuery(id+"F0.wireOp",EDGE,"E327"),sQuery(id+"F0.wireOp",EDGE,"E328"),sQuery(id+"F0.wireOp",EDGE,"E329"),sQuery(id+"F0.wireOp",EDGE,"E330"),sQuery(id+"F0.wireOp",EDGE,"E331"),sQuery(id+"F0.wireOp",EDGE,"E332"),sQuery(id+"F0.wireOp",EDGE,"E333"),sQuery(id+"F0.wireOp",EDGE,"E334"),sQuery(id+"F0.wireOp",EDGE,"E335"),sQuery(id+"F0.wireOp",EDGE,"E336"),sQuery(id+"F0.wireOp",EDGE,"E337"),sQuery(id+"F0.wireOp",EDGE,"E338"),sQuery(id+"F0.wireOp",EDGE,"E339"),sQuery(id+"F0.wireOp",EDGE,"E340"),sQuery(id+"F0.wireOp",EDGE,"E341"),sQuery(id+"F0.wireOp",EDGE,"E342"),sQuery(id+"F0.wireOp",EDGE,"E343"),sQuery(id+"F0.wireOp",EDGE,"E344"),sQuery(id+"F0.wireOp",EDGE,"E345"),sQuery(id+"F0.wireOp",EDGE,"E346"),sQuery(id+"F0.wireOp",EDGE,"E347"),sQuery(id+"F0.wireOp",EDGE,"E348"),sQuery(id+"F0.wireOp",EDGE,"E349"),sQuery(id+"F0.wireOp",EDGE,"E350"),sQuery(id+"F0.wireOp",EDGE,"E351"),sQuery(id+"F0.wireOp",EDGE,"E352"),sQuery(id+"F0.wireOp",EDGE,"E353"),sQuery(id+"F0.wireOp",EDGE,"E354"),sQuery(id+"F0.wireOp",EDGE,"E355"),sQuery(id+"F0.wireOp",EDGE,"E356"),sQuery(id+"F0.wireOp",EDGE,"E359"),sQuery(id+"F0.wireOp",EDGE,"E360"),sQuery(id+"F0.wireOp",EDGE,"E361"),sQuery(id+"F0.wireOp",EDGE,"E362"),sQuery(id+"F0.wireOp",EDGE,"E363"),sQuery(id+"F0.wireOp",EDGE,"E364"),sQuery(id+"F0.wireOp",EDGE,"E368"),sQuery(id+"F0.wireOp",EDGE,"E370"),sQuery(id+"F0.wireOp",EDGE,"E374"),sQuery(id+"F0.wireOp",EDGE,"E408"),sQuery(id+"F0.wireOp",EDGE,"E409"),sQuery(id+"F0.wireOp",EDGE,"E410"),sQuery(id+"F0.wireOp",EDGE,"E411"),sQuery(id+"F0.wireOp",EDGE,"E412"),sQuery(id+"F0.wireOp",EDGE,"E413"),sQuery(id+"F0.wireOp",EDGE,"E414"),sQuery(id+"F0.wireOp",EDGE,"E415"),sQuery(id+"F0.wireOp",EDGE,"E416"),sQuery(id+"F0.wireOp",EDGE,"E417"),sQuery(id+"F0.wireOp",EDGE,"E418"),sQuery(id+"F0.wireOp",EDGE,"E419"),sQuery(id+"F0.wireOp",EDGE,"E420"),sQuery(id+"F0.wireOp",EDGE,"E421"),sQuery(id+"F0.wireOp",EDGE,"E422"),sQuery(id+"F0.wireOp",EDGE,"E423"),sQuery(id+"F0.wireOp",EDGE,"E424"),sQuery(id+"F0.wireOp",EDGE,"E425"),sQuery(id+"F0.wireOp",EDGE,"E426"),sQuery(id+"F0.wireOp",EDGE,"E427"),sQuery(id+"F0.wireOp",EDGE,"E428"),sQuery(id+"F0.wireOp",EDGE,"E429"),sQuery(id+"F0.wireOp",EDGE,"E430"),sQuery(id+"F0.wireOp",EDGE,"E431"),sQuery(id+"F0.wireOp",EDGE,"E432"),sQuery(id+"F0.wireOp",EDGE,"E433"),sQuery(id+"F0.wireOp",EDGE,"E434"),sQuery(id+"F0.wireOp",EDGE,"E435"),sQuery(id+"F0.wireOp",EDGE,"E436"),sQuery(id+"F0.wireOp",EDGE,"E437"),sQuery(id+"F0.wireOp",EDGE,"E438"),sQuery(id+"F0.wireOp",EDGE,"E439"),sQuery(id+"F0.wireOp",EDGE,"E440"),sQuery(id+"F0.wireOp",EDGE,"E441"),sQuery(id+"F0.wireOp",EDGE,"E442"),sQuery(id+"F0.wireOp",EDGE,"E443"),sQuery(id+"F0.wireOp",EDGE,"E444"),sQuery(id+"F0.wireOp",EDGE,"E445"),sQuery(id+"F0.wireOp",EDGE,"E446"),sQuery(id+"F0.wireOp",EDGE,"E447"),sQuery(id+"F0.wireOp",EDGE,"E448"),sQuery(id+"F0.wireOp",EDGE,"E449"),sQuery(id+"F0.wireOp",EDGE,"E450"),sQuery(id+"F0.wireOp",EDGE,"E451"),sQuery(id+"F0.wireOp",EDGE,"E452"),sQuery(id+"F0.wireOp",EDGE,"E453"),sQuery(id+"F0.wireOp",EDGE,"E454"),sQuery(id+"F0.wireOp",EDGE,"E455"),sQuery(id+"F0.wireOp",EDGE,"E456"),sQuery(id+"F0.wireOp",EDGE,"E457"),sQuery(id+"F0.wireOp",EDGE,"E458"),sQuery(id+"F0.wireOp",EDGE,"E459"),sQuery(id+"F0.wireOp",EDGE,"E460"),sQuery(id+"F0.wireOp",EDGE,"E461"),sQuery(id+"F0.wireOp",EDGE,"E462"),sQuery(id+"F0.wireOp",EDGE,"E463"),sQuery(id+"F0.wireOp",EDGE,"E464"),sQuery(id+"F0.wireOp",EDGE,"E465"),sQuery(id+"F0.wireOp",EDGE,"E466"),sQuery(id+"F0.wireOp",EDGE,"E467"),sQuery(id+"F0.wireOp",EDGE,"E468"),sQuery(id+"F0.wireOp",EDGE,"E469"),sQuery(id+"F0.wireOp",EDGE,"E470"),sQuery(id+"F0.wireOp",EDGE,"E471"),sQuery(id+"F0.wireOp",EDGE,"E472"),sQuery(id+"F0.wireOp",EDGE,"E473"),sQuery(id+"F0.wireOp",EDGE,"E474"),sQuery(id+"F0.wireOp",EDGE,"E475"),sQuery(id+"F0.wireOp",EDGE,"E476"),sQuery(id+"F0.wireOp",EDGE,"E477"),sQuery(id+"F0.wireOp",EDGE,"E478"),sQuery(id+"F0.wireOp",EDGE,"E479"),sQuery(id+"F0.wireOp",EDGE,"E480"),sQuery(id+"F0.wireOp",EDGE,"E481"),sQuery(id+"F0.wireOp",EDGE,"E482"),sQuery(id+"F0.wireOp",EDGE,"E483"),sQuery(id+"F0.wireOp",EDGE,"E484"),sQuery(id+"F0.wireOp",EDGE,"E485"),sQuery(id+"F0.wireOp",EDGE,"E486"),sQuery(id+"F0.wireOp",EDGE,"E487"),sQuery(id+"F0.wireOp",EDGE,"E488"),sQuery(id+"F0.wireOp",EDGE,"E489"),sQuery(id+"F0.wireOp",EDGE,"E490"),sQuery(id+"F0.wireOp",EDGE,"E491"),sQuery(id+"F0.wireOp",EDGE,"E492"),sQuery(id+"F0.wireOp",EDGE,"E493"),sQuery(id+"F0.wireOp",EDGE,"E494"),sQuery(id+"F0.wireOp",EDGE,"E495"),sQuery(id+"F0.wireOp",EDGE,"E496"),sQuery(id+"F0.wireOp",EDGE,"E497"),sQuery(id+"F0.wireOp",EDGE,"E498"),sQuery(id+"F0.wireOp",EDGE,"E499"),sQuery(id+"F0.wireOp",EDGE,"E500"),sQuery(id+"F0.wireOp",EDGE,"E501"),sQuery(id+"F0.wireOp",EDGE,"E502"),sQuery(id+"F0.wireOp",EDGE,"E503"),sQuery(id+"F0.wireOp",EDGE,"E504"),sQuery(id+"F0.wireOp",EDGE,"E505"),sQuery(id+"F0.wireOp",EDGE,"E506"),sQuery(id+"F0.wireOp",EDGE,"E507"),sQuery(id+"F0.wireOp",EDGE,"E508"),sQuery(id+"F0.wireOp",EDGE,"E509"),sQuery(id+"F0.wireOp",EDGE,"E510"),sQuery(id+"F0.wireOp",EDGE,"E511"),sQuery(id+"F0.wireOp",EDGE,"E512"),sQuery(id+"F0.wireOp",EDGE,"E513"),sQuery(id+"F0.wireOp",EDGE,"E514"),sQuery(id+"F0.wireOp",EDGE,"E515"),sQuery(id+"F0.wireOp",EDGE,"E516"),sQuery(id+"F0.wireOp",EDGE,"E517"),sQuery(id+"F0.wireOp",EDGE,"E518"),sQuery(id+"F0.wireOp",EDGE,"E519"),sQuery(id+"F0.wireOp",EDGE,"E520"),sQuery(id+"F0.wireOp",EDGE,"E521"),sQuery(id+"F0.wireOp",EDGE,"E522"),sQuery(id+"F0.wireOp",EDGE,"E523"),sQuery(id+"F0.wireOp",EDGE,"E524"),sQuery(id+"F0.wireOp",EDGE,"E525"),sQuery(id+"F0.wireOp",EDGE,"E526"),sQuery(id+"F0.wireOp",EDGE,"E527"),sQuery(id+"F0.wireOp",EDGE,"E528"),sQuery(id+"F0.wireOp",EDGE,"E529"),sQuery(id+"F0.wireOp",EDGE,"E530"),sQuery(id+"F0.wireOp",EDGE,"E531"),sQuery(id+"F0.wireOp",EDGE,"E532"),sQuery(id+"F0.wireOp",EDGE,"E533"),sQuery(id+"F0.wireOp",EDGE,"E534"),sQuery(id+"F0.wireOp",EDGE,"E535"),sQuery(id+"F0.wireOp",EDGE,"E536"),sQuery(id+"F0.wireOp",EDGE,"E537"),sQuery(id+"F0.wireOp",EDGE,"E538"),sQuery(id+"F0.wireOp",EDGE,"E539"),sQuery(id+"F0.wireOp",EDGE,"E540"),sQuery(id+"F0.wireOp",EDGE,"E541"),sQuery(id+"F0.wireOp",EDGE,"E542"),sQuery(id+"F0.wireOp",EDGE,"E543"),sQuery(id+"F0.wireOp",EDGE,"E544"),sQuery(id+"F0.wireOp",EDGE,"E545"),sQuery(id+"F0.wireOp",EDGE,"E546"),sQuery(id+"F0.wireOp",EDGE,"E547"),sQuery(id+"F0.wireOp",EDGE,"E548"),sQuery(id+"F0.wireOp",EDGE,"E549"),sQuery(id+"F0.wireOp",EDGE,"E550"),sQuery(id+"F0.wireOp",EDGE,"E551"),sQuery(id+"F0.wireOp",EDGE,"E552"),sQuery(id+"F0.wireOp",EDGE,"E553"),sQuery(id+"F0.wireOp",EDGE,"E554"),sQuery(id+"F0.wireOp",EDGE,"E555"),sQuery(id+"F0.wireOp",EDGE,"E556"),sQuery(id+"F0.wireOp",EDGE,"E557"),sQuery(id+"F0.wireOp",EDGE,"E558"),sQuery(id+"F0.wireOp",EDGE,"E559"),sQuery(id+"F0.wireOp",EDGE,"E560"),sQuery(id+"F0.wireOp",EDGE,"E561"),sQuery(id+"F0.wireOp",EDGE,"E562"),sQuery(id+"F0.wireOp",EDGE,"E563"),sQuery(id+"F0.wireOp",EDGE,"E564"),sQuery(id+"F0.wireOp",EDGE,"E565"),sQuery(id+"F0.wireOp",EDGE,"E566"),sQuery(id+"F0.wireOp",EDGE,"E567"),sQuery(id+"F0.wireOp",EDGE,"E568"),sQuery(id+"F0.wireOp",EDGE,"E569"),sQuery(id+"F0.wireOp",EDGE,"E570"),sQuery(id+"F0.wireOp",EDGE,"E571"),sQuery(id+"F0.wireOp",EDGE,"E572"),sQuery(id+"F0.wireOp",EDGE,"E573"),sQuery(id+"F0.wireOp",EDGE,"E574"),sQuery(id+"F0.wireOp",EDGE,"E575"),sQuery(id+"F0.wireOp",EDGE,"E576"),sQuery(id+"F0.wireOp",EDGE,"E577"),sQuery(id+"F0.wireOp",EDGE,"E578"),sQuery(id+"F0.wireOp",EDGE,"E579"),sQuery(id+"F0.wireOp",EDGE,"E580"),sQuery(id+"F0.wireOp",EDGE,"E581"),sQuery(id+"F0.wireOp",EDGE,"E582"),sQuery(id+"F0.wireOp",EDGE,"E583"),sQuery(id+"F0.wireOp",EDGE,"E584"),sQuery(id+"F0.wireOp",EDGE,"E585"),sQuery(id+"F0.wireOp",EDGE,"E586"),sQuery(id+"F0.wireOp",EDGE,"E587"),sQuery(id+"F0.wireOp",EDGE,"E588"),sQuery(id+"F0.wireOp",EDGE,"E589"),sQuery(id+"F0.wireOp",EDGE,"E590"),sQuery(id+"F0.wireOp",EDGE,"E591"),sQuery(id+"F0.wireOp",EDGE,"E592"),sQuery(id+"F0.wireOp",EDGE,"E597"),sQuery(id+"F0.wireOp",EDGE,"E599"),sQuery(id+"F0.wireOp",EDGE,"E600"),sQuery(id+"F0.wireOp",EDGE,"E601"),sQuery(id+"F0.wireOp",EDGE,"E604"),sQuery(id+"F0.wireOp",EDGE,"E605"),sQuery(id+"F0.wireOp",EDGE,"E606"),sQuery(id+"F0.wireOp",EDGE,"E607"),sQuery(id+"F0.wireOp",EDGE,"E608"),sQuery(id+"F0.wireOp",EDGE,"E609"),sQuery(id+"F0.wireOp",EDGE,"E612"),sQuery(id+"F0.wireOp",EDGE,"E614"),sQuery(id+"F0.wireOp",EDGE,"E615"),sQuery(id+"F0.wireOp",EDGE,"E616"),sQuery(id+"F0.wireOp",EDGE,"E617"),sQuery(id+"F0.wireOp",EDGE,"E618"),sQuery(id+"F0.wireOp",EDGE,"E619"),sQuery(id+"F0.wireOp",EDGE,"E620"),sQuery(id+"F0.wireOp",EDGE,"E621"),sQuery(id+"F0.wireOp",EDGE,"E622"),sQuery(id+"F0.wireOp",EDGE,"E623"),sQuery(id+"F0.wireOp",EDGE,"E624"),sQuery(id+"F0.wireOp",EDGE,"E625"),sQuery(id+"F0.wireOp",EDGE,"E626"),sQuery(id+"F0.wireOp",EDGE,"E627"),sQuery(id+"F0.wireOp",EDGE,"E628"),sQuery(id+"F0.wireOp",EDGE,"E629"),sQuery(id+"F0.wireOp",EDGE,"E630"),sQuery(id+"F0.wireOp",EDGE,"E635"),sQuery(id+"F0.wireOp",EDGE,"E636"),sQuery(id+"F0.wireOp",EDGE,"E638"),sQuery(id+"F0.wireOp",EDGE,"E639"),sQuery(id+"F0.wireOp",EDGE,"E640"),sQuery(id+"F0.wireOp",EDGE,"E641"),sQuery(id+"F0.wireOp",EDGE,"E642"),sQuery(id+"F0.wireOp",EDGE,"E643"),sQuery(id+"F0.wireOp",EDGE,"E644"),sQuery(id+"F0.wireOp",EDGE,"E645"),sQuery(id+"F0.wireOp",EDGE,"E646"),sQuery(id+"F0.wireOp",EDGE,"E653"),sQuery(id+"F0.wireOp",EDGE,"E654"),sQuery(id+"F0.wireOp",EDGE,"E655"),sQuery(id+"F0.wireOp",EDGE,"E656"),sQuery(id+"F0.wireOp",EDGE,"E657"),sQuery(id+"F0.wireOp",EDGE,"E658"),sQuery(id+"F0.wireOp",EDGE,"E659"),sQuery(id+"F0.wireOp",EDGE,"E660"),sQuery(id+"F0.wireOp",EDGE,"E661"),sQuery(id+"F0.wireOp",EDGE,"E662"),sQuery(id+"F0.wireOp",EDGE,"E663"),sQuery(id+"F0.wireOp",EDGE,"E664"),sQuery(id+"F0.wireOp",EDGE,"E665"),sQuery(id+"F0.wireOp",EDGE,"E666"),sQuery(id+"F0.wireOp",EDGE,"E667"),sQuery(id+"F0.wireOp",EDGE,"E668"),sQuery(id+"F0.wireOp",EDGE,"E669"),sQuery(id+"F0.wireOp",EDGE,"E670"),sQuery(id+"F0.wireOp",EDGE,"E671"),sQuery(id+"F0.wireOp",EDGE,"E672"),sQuery(id+"F0.wireOp",EDGE,"E673"),sQuery(id+"F0.wireOp",EDGE,"E674")])],"isStart":true});
            var sketch = newSketch(context, id + "F4", { "sketchPlane" : qUnion([Q0])});
            skCircle(sketch, "E680", {"center": v(14, 0) * mm, "radius": 18.5 * mm});
            skLineSegment(sketch, "E681", {"start": v(35.33, 0) * mm, "end": v(-7.33, 0) * mm});
            skSolve(sketch);
        }
        {
            var Q0;
            Q0=qSketchRegion(id+"F4",true);
            extrude(context, id + "F5", {"entities" : qUnion([Q0]), "operationType" : NewBodyOperationType.ADD, "depth" : 24.1 * mm, "offsetDistance" : 25 * mm});
        }
        {
            var Q0;
            Q0=makeQuery(id+"F5.opExtrude","CAP_FACE",FACE,{"disambiguationData":[OSD([sQuery(id+"F4.wireOp",EDGE,"E680")])],"isStart":false});
            var sketch = newSketch(context, id + "F6", { "sketchPlane" : qUnion([Q0])});
            skLineSegment(sketch, "E682", {"start": v(32.5, 0) * mm, "end": v(-4.5, 0) * mm, "construction": true});
            skLineSegment(sketch, "E683.bottom", {"start": v(0, -1.7) * mm, "end": v(28, -1.7) * mm});
            skLineSegment(sketch, "E683.top", {"start": v(0, 1.7) * mm, "end": v(28, 1.7) * mm});
            skLineSegment(sketch, "E683.left", {"start": v(0, -1.7) * mm, "end": v(0, 1.7) * mm});
            skLineSegment(sketch, "E683.right", {"start": v(28, -1.7) * mm, "end": v(28, 1.7) * mm});
            skPoint(sketch, "E683.middle", {"position": v(14, 0) * mm});
            skSolve(sketch);
        }
        {
            var Q0;
            Q0=qSketchRegion(id+"F6",true);
            extrude(context, id + "F7", {"entities" : qUnion([Q0]), "operationType" : NewBodyOperationType.REMOVE, "oppositeDirection" : true, "depth" : 32 * mm, "offsetDistance" : 25 * mm});
        }
        {
            var Q0;
            Q0=makeQuery(id+"F3.opExtrude","CAP_FACE",FACE,{"disambiguationData":[OSD([sQuery(id+"F2.wireOp",EDGE,"E679")])],"isStart":false});
            var sketch = newSketch(context, id + "F8", { "sketchPlane" : qUnion([Q0])});
            skCircle(sketch, "E684", {"center": v(14, 10) * mm, "radius": 1.85 * mm});
            skCircle(sketch, "E685", {"center": v(14, -10) * mm, "radius": 1.85 * mm});
            skPoint(sketch, "E686.0", {"position": v(14, 1.7) * mm});
            skPoint(sketch, "E687.0", {"position": v(28, 0) * mm});
            skLineSegment(sketch, "E688", {"start": v(28, 0) * mm, "end": v(22.31, 0) * mm, "construction": true});
            skSolve(sketch);
        }
        {
            var Q0;
            Q0=qSketchRegion(id+"F8",true);
            extrude(context, id + "F9", {"entities" : qUnion([Q0]), "operationType" : NewBodyOperationType.REMOVE, "oppositeDirection" : true, "depth" : 21 * mm, "offsetDistance" : 25 * mm});
        }
    });
